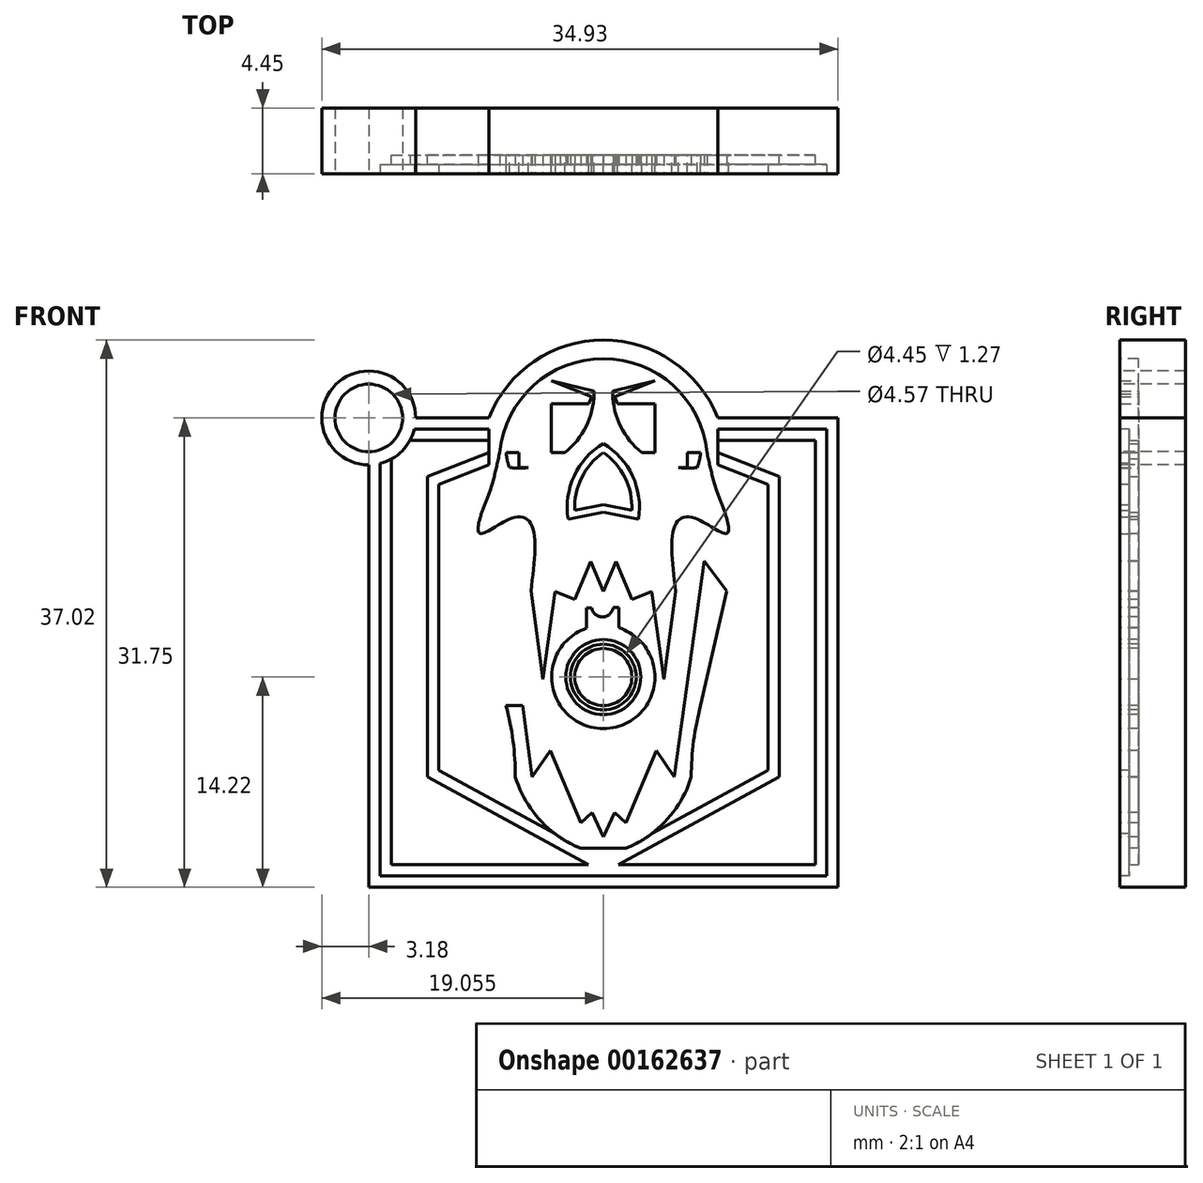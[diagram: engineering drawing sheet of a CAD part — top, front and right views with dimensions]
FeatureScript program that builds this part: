
annotation { "Feature Type Name" : "Feature", "Feature Type Description" : "" }
export const myFeature = defineFeature(function(context is Context, id is Id, definition is map)
    precondition{}
    {
        {
            var Q0;
            Q0=qCreatedBy(makeId("Front.planeOp"),FACE);
            var sketch = newSketch(context, id + "F0", { "sketchPlane" : qUnion([Q0])});
            skLineSegment(sketch, "E0", {"start": v(0, 0) * mm, "end": v(0, 31.75) * mm});
            skLineSegment(sketch, "E1", {"start": v(0, 31.75) * mm, "end": v(31.75, 31.75) * mm});
            skLineSegment(sketch, "E2", {"start": v(31.75, 31.75) * mm, "end": v(31.75, 0) * mm});
            skLineSegment(sketch, "E3", {"start": v(31.75, 0) * mm, "end": v(0, 0) * mm});
            skSolve(sketch);
        }
        {
            var Q0;
            Q0 = qSketchRegion(id + "F0", true);
            extrude(context, id + "F1", {"entities" : qUnion([Q0]), "depth" : 3.17 * mm});
        }
        {
            var Q0;
            Q0=makeQuery(id+"F1.opExtrude","CAP_FACE",FACE,{"disambiguationData":[OSD([sQuery(id+"F0.wireOp",EDGE,"E0"),sQuery(id+"F0.wireOp",EDGE,"E1"),sQuery(id+"F0.wireOp",EDGE,"E2"),sQuery(id+"F0.wireOp",EDGE,"E3")])],"isStart":false});
            var sketch = newSketch(context, id + "F2", { "sketchPlane" : qUnion([Q0])});
            skLineSegment(sketch, "E4", {"start": v(0, 0) * mm, "end": v(15.88, 0) * mm});
            skPoint(sketch, "E5.orphan", {"position": v(0, 15.88) * mm});
            skPoint(sketch, "E6.end.orphan", {"position": v(7.94, 3.97) * mm});
            skPoint(sketch, "E7.start.orphan", {"position": v(0, 7.94) * mm});
            skLineSegment(sketch, "E8", {"start": v(0, 31.75) * mm, "end": v(1.52, 31.75) * mm});
            skLineSegment(sketch, "E9", {"start": v(1.52, 30.23) * mm, "end": v(1.52, 1.52) * mm});
            skLineSegment(sketch, "E10", {"start": v(0, 31.75) * mm, "end": v(0, 27.78) * mm});
            skLineSegment(sketch, "E11.bottom", {"start": v(0, 31.75) * mm, "end": v(31.75, 31.75) * mm});
            skLineSegment(sketch, "E11.top", {"start": v(0, 0) * mm, "end": v(31.75, 0) * mm});
            skLineSegment(sketch, "E11.left", {"start": v(0, 31.75) * mm, "end": v(0, 0) * mm});
            skLineSegment(sketch, "E11.right", {"start": v(31.75, 31.75) * mm, "end": v(31.75, 0) * mm});
            skLineSegment(sketch, "E12.2", {"start": v(30.23, 1.52) * mm, "end": v(30.23, 30.23) * mm});
            skLineSegment(sketch, "E12.3", {"start": v(1.52, 1.52) * mm, "end": v(14.86, 1.52) * mm});
            skPoint(sketch, "E13.orphan", {"position": v(3.97, 31.75) * mm});
            skPoint(sketch, "E14.orphan", {"position": v(15.88, 31.75) * mm});
            skPoint(sketch, "E15.orphan", {"position": v(27.78, 31.75) * mm});
            skPoint(sketch, "E16.orphan", {"position": v(15.88, 0) * mm});
            skLineSegment(sketch, "E17.trimOffspring", {"start": v(16.9, 1.52) * mm, "end": v(30.23, 1.52) * mm});
            skLineSegment(sketch, "E18", {"start": v(3.97, 27.78) * mm, "end": v(3.97, 7.46) * mm});
            skLineSegment(sketch, "E19", {"start": v(27.78, 27.78) * mm, "end": v(27.78, 7.46) * mm});
            skLineSegment(sketch, "E20", {"start": v(3.97, 7.46) * mm, "end": v(14.86, 1.52) * mm});
            skLineSegment(sketch, "E21", {"start": v(27.78, 7.46) * mm, "end": v(16.9, 1.52) * mm});
            skPoint(sketch, "E22.orphan", {"position": v(20.45, 30.23) * mm});
            skPoint(sketch, "E23.orphan", {"position": v(11.3, 30.23) * mm});
            skLineSegment(sketch, "E24", {"start": v(1.52, 30.23) * mm, "end": v(8.13, 30.23) * mm});
            skLineSegment(sketch, "E25", {"start": v(30.23, 30.23) * mm, "end": v(23.62, 30.23) * mm});
            skLineSegment(sketch, "E26", {"start": v(8.13, 30.23) * mm, "end": v(8.13, 29.41) * mm});
            skLineSegment(sketch, "E27", {"start": v(8.13, 29.41) * mm, "end": v(3.97, 27.78) * mm});
            skLineSegment(sketch, "E28", {"start": v(23.62, 30.23) * mm, "end": v(23.62, 29.41) * mm});
            skLineSegment(sketch, "E29", {"start": v(23.62, 29.41) * mm, "end": v(27.78, 27.78) * mm});
            skSolve(sketch);
        }
        {
            var Q0;
            Q0 = qSketchRegion(id + "F2", true);
            extrude(context, id + "F3", {"entities" : qUnion([Q0]), "operationType" : NewBodyOperationType.ADD, "depth" : 1.27 * mm});
        }
        {
            var Q0;
            Q0=makeQuery(id+"F3.opExtrude","CAP_FACE",FACE,{"disambiguationData":[OSD([sQuery(id+"F2.wireOp",EDGE,"E9"),sQuery(id+"F2.wireOp",EDGE,"goVl8tom-Ev7d-GRHB-ppSx-mnuqSaHJAKLd"),sQuery(id+"F2.wireOp",EDGE,"1ae28c5b-480c-4ecc-ba1d-f622eb84b6210.MirrorCS"),sQuery(id+"F2.wireOp",EDGE,"E11.bottom"),sQuery(id+"F2.wireOp",EDGE,"E11.top"),sQuery(id+"F2.wireOp",EDGE,"E11.left"),sQuery(id+"F2.wireOp",EDGE,"E11.right"),sQuery(id+"F2.wireOp",EDGE,"E12.1"),sQuery(id+"F2.wireOp",EDGE,"E12.2"),sQuery(id+"F2.wireOp",EDGE,"E12.3"),sQuery(id+"F2.wireOp",EDGE,"3f8098f8-ebf5-42e8-aa49-ce20f5d09108.trimOffspring"),sQuery(id+"F2.wireOp",EDGE,"E17.trimOffspring"),sQuery(id+"F2.wireOp",EDGE,"E18"),sQuery(id+"F2.wireOp",EDGE,"E19"),sQuery(id+"F2.wireOp",EDGE,"E20"),sQuery(id+"F2.wireOp",EDGE,"E21"),sQuery(id+"F2.wireOp",EDGE,"gHRPagYE-y3ma-9N2y-mR8m-tlt3Iz92IcqW"),sQuery(id+"F2.wireOp",EDGE,"vgOmxDC5-mCE1-dIMU-f8gZ-2gwDJ6tH9BS1"),sQuery(id+"F2.wireOp",EDGE,"jJyTZG4A-tfUV-d1xE-bx1D-zMVtqKziVOon"),sQuery(id+"F2.wireOp",EDGE,"4SgWYagR-BqLy-cmup-oolx-HVRRYwsgYGB8")])],"isStart":false});
            var sketch = newSketch(context, id + "F4", { "sketchPlane" : qUnion([Q0])});
            skLineSegment(sketch, "E30", {"start": v(3.97, 7.46) * mm, "end": v(13.05, 7.46) * mm});
            skLineSegment(sketch, "E31", {"start": v(3.97, 7.46) * mm, "end": v(14.86, 1.52) * mm});
            skLineSegment(sketch, "E32", {"start": v(16.9, 1.52) * mm, "end": v(27.78, 7.46) * mm});
            skLineSegment(sketch, "E33", {"start": v(15.88, 2.63) * mm, "end": v(14.36, 2.63) * mm});
            skLineSegment(sketch, "E34", {"start": v(15.88, 2.63) * mm, "end": v(17.4, 2.63) * mm});
            skPoint(sketch, "E35.end.orphan", {"position": v(15.88, 1.52) * mm});
            skPoint(sketch, "E35.start.orphan", {"position": v(15.88, 0) * mm});
            skLineSegment(sketch, "E36", {"start": v(9.92, 7.46) * mm, "end": v(9.92, 4.22) * mm});
            skLineSegment(sketch, "E37", {"start": v(27.78, 7.46) * mm, "end": v(15.88, 7.46) * mm});
            skLineSegment(sketch, "E38", {"start": v(21.83, 7.46) * mm, "end": v(21.83, 4.22) * mm});
            skPoint(sketch, "E39.end.orphan", {"position": v(15.88, 3.73) * mm});
            skLineSegment(sketch, "E40", {"start": v(3.97, 7.46) * mm, "end": v(3.97, 12.29) * mm});
            skLineSegment(sketch, "E41", {"start": v(3.97, 12.29) * mm, "end": v(12.97, 12.29) * mm});
            skLineSegment(sketch, "E42", {"start": v(9.92, 7.46) * mm, "end": v(9.92, 12.29) * mm});
            skLineSegment(sketch, "E43", {"start": v(21.83, 7.46) * mm, "end": v(21.83, 12.29) * mm});
            skLineSegment(sketch, "E44", {"start": v(3.97, 27.78) * mm, "end": v(3.97, 12.29) * mm});
            skLineSegment(sketch, "E45", {"start": v(9.92, 12.29) * mm, "end": v(9.29, 12.29) * mm});
            skLineSegment(sketch, "E46", {"start": v(21.83, 12.29) * mm, "end": v(22.46, 12.29) * mm});
            skArc(sketch, "E47", {"start": v(9.92, 7.46) * mm, "mid": v(9.76, 9.9) * mm, "end": v(9.29, 12.29) * mm});
            skArc(sketch, "E48", {"start": v(22.46, 12.29) * mm, "mid": v(21.99, 9.9) * mm, "end": v(21.83, 7.46) * mm});
            skLineSegment(sketch, "E49", {"start": v(3.97, 20.03) * mm, "end": v(7.52, 20.03) * mm});
            skLineSegment(sketch, "E50", {"start": v(27.78, 20.03) * mm, "end": v(27.78, 12.29) * mm});
            skLineSegment(sketch, "E51", {"start": v(7.52, 20.03) * mm, "end": v(9.29, 12.29) * mm});
            skLineSegment(sketch, "E52", {"start": v(27.78, 20.03) * mm, "end": v(24.23, 20.03) * mm});
            skLineSegment(sketch, "E53", {"start": v(24.23, 20.03) * mm, "end": v(22.46, 12.29) * mm});
            skLineSegment(sketch, "E54", {"start": v(7.52, 20.03) * mm, "end": v(9.06, 22.06) * mm});
            skLineSegment(sketch, "E55", {"start": v(24.23, 20.03) * mm, "end": v(22.7, 22.06) * mm});
            skLineSegment(sketch, "E56", {"start": v(9.06, 22.06) * mm, "end": v(11.06, 7.46) * mm});
            skLineSegment(sketch, "E57", {"start": v(22.7, 22.06) * mm, "end": v(20.69, 7.46) * mm});
            skLineSegment(sketch, "E58", {"start": v(15.88, 2.63) * mm, "end": v(15.88, 3.39) * mm});
            skLineSegment(sketch, "E59", {"start": v(15.88, 7.46) * mm, "end": v(13.94, 7.46) * mm});
            skLineSegment(sketch, "E60", {"start": v(3.97, 7.46) * mm, "end": v(6.69, 5.98) * mm});
            skLineSegment(sketch, "E61", {"start": v(15.88, 7.46) * mm, "end": v(20.69, 7.46) * mm});
            skLineSegment(sketch, "E62", {"start": v(14.36, 2.63) * mm, "end": v(14.36, 4.36) * mm});
            skArc(sketch, "E63", {"start": v(9.92, 7.46) * mm, "mid": v(11.6, 4.54) * mm, "end": v(14.36, 2.63) * mm});
            skLineSegment(sketch, "E64", {"start": v(17.4, 2.63) * mm, "end": v(17.4, 4.36) * mm});
            skArc(sketch, "E65", {"start": v(17.4, 2.63) * mm, "mid": v(20.16, 4.54) * mm, "end": v(21.83, 7.46) * mm});
            skLineSegment(sketch, "E66", {"start": v(11.06, 7.46) * mm, "end": v(11.06, 5.19) * mm});
            skLineSegment(sketch, "E67", {"start": v(20.69, 7.46) * mm, "end": v(20.69, 5.19) * mm});
            skLineSegment(sketch, "E68", {"start": v(14.36, 7.46) * mm, "end": v(11.06, 7.46) * mm});
            skLineSegment(sketch, "E69", {"start": v(12.7, 7.46) * mm, "end": v(12.7, 3.54) * mm});
            skLineSegment(sketch, "E70", {"start": v(17.4, 7.46) * mm, "end": v(20.69, 7.46) * mm});
            skLineSegment(sketch, "E71", {"start": v(19.04, 7.46) * mm, "end": v(19.04, 3.54) * mm});
            skLineSegment(sketch, "E72", {"start": v(11.06, 7.46) * mm, "end": v(12.7, 7.46) * mm});
            skLineSegment(sketch, "E73", {"start": v(14.36, 7.46) * mm, "end": v(12.7, 7.46) * mm});
            skLineSegment(sketch, "E74", {"start": v(13.53, 6.31) * mm, "end": v(13.53, 4.92) * mm});
            skLineSegment(sketch, "E75", {"start": v(20.69, 7.46) * mm, "end": v(19.04, 7.46) * mm});
            skLineSegment(sketch, "E76", {"start": v(19.04, 7.46) * mm, "end": v(17.4, 7.46) * mm});
            skLineSegment(sketch, "E77", {"start": v(11.06, 5.19) * mm, "end": v(12.7, 5.19) * mm});
            skLineSegment(sketch, "E78", {"start": v(12.7, 5.19) * mm, "end": v(12.7, 3.54) * mm});
            skLineSegment(sketch, "E79", {"start": v(12.7, 4.36) * mm, "end": v(11.76, 4.36) * mm});
            skLineSegment(sketch, "E80", {"start": v(12.7, 7.46) * mm, "end": v(13.05, 7.46) * mm});
            skLineSegment(sketch, "E81", {"start": v(13.12, 7.29) * mm, "end": v(13.12, 3.26) * mm});
            skLineSegment(sketch, "E82", {"start": v(12.7, 4.36) * mm, "end": v(13.12, 4.36) * mm});
            skLineSegment(sketch, "E83", {"start": v(19.04, 7.46) * mm, "end": v(18.22, 7.46) * mm});
            skLineSegment(sketch, "E84", {"start": v(18.63, 7.29) * mm, "end": v(18.63, 3.26) * mm});
            skLineSegment(sketch, "E85", {"start": v(20.69, 5.19) * mm, "end": v(19.04, 5.19) * mm});
            skLineSegment(sketch, "E86", {"start": v(19.04, 5.19) * mm, "end": v(19.04, 3.54) * mm});
            skLineSegment(sketch, "E87", {"start": v(19.04, 4.36) * mm, "end": v(19.99, 4.36) * mm});
            skLineSegment(sketch, "E88", {"start": v(19.04, 4.36) * mm, "end": v(18.63, 4.36) * mm});
            skLineSegment(sketch, "E89", {"start": v(13.53, 7.46) * mm, "end": v(14.36, 7.46) * mm});
            skLineSegment(sketch, "E90", {"start": v(13.94, 5.34) * mm, "end": v(13.94, 2.8) * mm});
            skLineSegment(sketch, "E91", {"start": v(18.22, 7.46) * mm, "end": v(17.4, 7.46) * mm});
            skLineSegment(sketch, "E92", {"start": v(17.8, 5.34) * mm, "end": v(17.8, 2.8) * mm});
            skLineSegment(sketch, "E93", {"start": v(18.22, 6.31) * mm, "end": v(18.22, 4.92) * mm});
            skLineSegment(sketch, "E94", {"start": v(11.89, 7.46) * mm, "end": v(12.7, 7.46) * mm});
            skLineSegment(sketch, "E95", {"start": v(12.3, 7.46) * mm, "end": v(12.3, 9.24) * mm});
            skLineSegment(sketch, "E96", {"start": v(13.12, 4.36) * mm, "end": v(14.36, 4.36) * mm});
            skLineSegment(sketch, "E97", {"start": v(18.63, 4.36) * mm, "end": v(17.4, 4.36) * mm});
            skLineSegment(sketch, "E98", {"start": v(15.88, 7.46) * mm, "end": v(15.88, 5.04) * mm});
            skLineSegment(sketch, "E99", {"start": v(19.86, 7.46) * mm, "end": v(19.04, 7.46) * mm});
            skLineSegment(sketch, "E100", {"start": v(19.45, 7.46) * mm, "end": v(19.45, 9.24) * mm});
            skPoint(sketch, "E100.endSnap0", {"position": v(19.45, 7.46) * mm});
            skLineSegment(sketch, "E101", {"start": v(13.53, 4.92) * mm, "end": v(13.53, 3.02) * mm});
            skPoint(sketch, "E102.endSnap0", {"position": v(13.74, 4.36) * mm});
            skLineSegment(sketch, "E103", {"start": v(18.22, 4.92) * mm, "end": v(18.22, 3.02) * mm});
            skPoint(sketch, "E104.orphan", {"position": v(12.84, 2.63) * mm});
            skPoint(sketch, "E105.orphan", {"position": v(18.91, 2.63) * mm});
            skLineSegment(sketch, "E106", {"start": v(15.88, 6.25) * mm, "end": v(15.88, 5.04) * mm});
            skLineSegment(sketch, "E107", {"start": v(15.88, 5.65) * mm, "end": v(15.88, 5.04) * mm});
            skLineSegment(sketch, "E108", {"start": v(14.36, 3.5) * mm, "end": v(12.7, 3.54) * mm});
            skLineSegment(sketch, "E109", {"start": v(19.04, 3.54) * mm, "end": v(17.4, 3.54) * mm});
            skLineSegment(sketch, "E110", {"start": v(20.69, 7.46) * mm, "end": v(19.45, 9.24) * mm});
            skLineSegment(sketch, "E111", {"start": v(15.88, 3.39) * mm, "end": v(16.63, 5.04) * mm});
            skLineSegment(sketch, "E112", {"start": v(11.06, 7.46) * mm, "end": v(12.3, 9.24) * mm});
            skLineSegment(sketch, "E113", {"start": v(15.12, 5.04) * mm, "end": v(15.88, 3.39) * mm});
            skLineSegment(sketch, "E114", {"start": v(15.12, 5.04) * mm, "end": v(14.36, 4.36) * mm});
            skLineSegment(sketch, "E115", {"start": v(12.3, 9.24) * mm, "end": v(14.36, 4.36) * mm});
            skLineSegment(sketch, "E116", {"start": v(16.63, 5.04) * mm, "end": v(17.4, 4.36) * mm});
            skLineSegment(sketch, "E117", {"start": v(17.4, 4.36) * mm, "end": v(19.45, 9.24) * mm});
            skLineSegment(sketch, "E118.trimOffspring", {"start": v(13.94, 7.46) * mm, "end": v(15.88, 7.46) * mm});
            skLineSegment(sketch, "E119.trimOffspring", {"start": v(13.94, 7.46) * mm, "end": v(27.78, 7.46) * mm});
            skPoint(sketch, "E120.orphan", {"position": v(13.12, 7.46) * mm});
            skLineSegment(sketch, "E121.trimOffspring", {"start": v(13.53, 7.46) * mm, "end": v(11.06, 7.46) * mm});
            skPoint(sketch, "E122.start.orphan", {"position": v(15.88, 5.35) * mm});
            skPoint(sketch, "E123.orphan", {"position": v(14.36, 5.04) * mm});
            skPoint(sketch, "E124.start.orphan", {"position": v(17.4, 5.04) * mm});
            skPoint(sketch, "E125.start.orphan", {"position": v(16.63, 3.84) * mm});
            skPoint(sketch, "E126.orphan", {"position": v(16.63, 4.44) * mm});
            skPoint(sketch, "E127.end.orphan", {"position": v(16.63, 2.63) * mm});
            skPoint(sketch, "E128.orphan", {"position": v(17.8, 7.46) * mm});
            skPoint(sketch, "E129.orphan", {"position": v(18.63, 7.46) * mm});
            skPoint(sketch, "E130.orphan", {"position": v(17.4, 4.44) * mm});
            skLineSegment(sketch, "E131.trimOffspring", {"start": v(24.23, 20.03) * mm, "end": v(27.78, 20.03) * mm});
            skCircle(sketch, "E132", {"center": v(15.87, 14.22) * mm, "radius": 1.93 * mm});
            skCircle(sketch, "E133", {"center": v(15.87, 14.22) * mm, "radius": 2.22 * mm});
            skCircle(sketch, "E134", {"center": v(15.87, 14.22) * mm, "radius": 2.54 * mm});
            skArc(sketch, "E135", {"start": v(14.72, 17.52) * mm, "mid": v(15.93, 10.73) * mm, "end": v(16.91, 17.55) * mm});
            skLineSegment(sketch, "E136.trimOffspring", {"start": v(18.78, 12.29) * mm, "end": v(27.78, 12.29) * mm});
            skLineSegment(sketch, "E137.trimOffspring", {"start": v(12.96, 12.3) * mm, "end": v(12.96, 12.29) * mm});
            skLineSegment(sketch, "E138.trimOffspring", {"start": v(18.79, 12.3) * mm, "end": v(18.79, 12.29) * mm});
            skLineSegment(sketch, "E139", {"start": v(15.02, 22.04) * mm, "end": v(15.87, 20.02) * mm});
            skLineSegment(sketch, "E140", {"start": v(16.73, 22.04) * mm, "end": v(15.87, 20.02) * mm});
            skLineSegment(sketch, "E141", {"start": v(10.97, 20.02) * mm, "end": v(11.79, 14.07) * mm});
            skLineSegment(sketch, "E142", {"start": v(20.78, 20.01) * mm, "end": v(19.96, 14.06) * mm});
            skLineSegment(sketch, "E143", {"start": v(11.79, 14.07) * mm, "end": v(12.6, 20.02) * mm});
            skLineSegment(sketch, "E144", {"start": v(19.96, 14.06) * mm, "end": v(19.14, 20.01) * mm});
            skLineSegment(sketch, "E145", {"start": v(17.61, 20.53) * mm, "end": v(17.69, 20.5) * mm});
            skPoint(sketch, "E146.endSnap0", {"position": v(13.94, 20.02) * mm});
            skLineSegment(sketch, "E147", {"start": v(12.6, 20.02) * mm, "end": v(13.94, 19.46) * mm});
            skPoint(sketch, "E148.endSnap0", {"position": v(17.8, 20.47) * mm});
            skLineSegment(sketch, "E149", {"start": v(17.8, 19.45) * mm, "end": v(19.14, 20.01) * mm});
            skLineSegment(sketch, "E150", {"start": v(14.72, 17.52) * mm, "end": v(14.72, 18.9) * mm});
            skLineSegment(sketch, "E151", {"start": v(14.72, 18.9) * mm, "end": v(15.1, 18.9) * mm});
            skLineSegment(sketch, "E152", {"start": v(16.91, 17.55) * mm, "end": v(16.91, 18.92) * mm});
            skLineSegment(sketch, "E153", {"start": v(16.91, 18.92) * mm, "end": v(16.54, 18.92) * mm});
            skArc(sketch, "E154", {"start": v(15.1, 18.9) * mm, "mid": v(15.83, 18.29) * mm, "end": v(16.54, 18.92) * mm});
            skPoint(sketch, "E155.orphan", {"position": v(9.34, 20.03) * mm});
            skPoint(sketch, "E156.orphan", {"position": v(22.4, 20) * mm});
            skPoint(sketch, "E157.orphan", {"position": v(15.87, 18.87) * mm});
            skPoint(sketch, "E158.orphan", {"position": v(14.2, 20.02) * mm});
            skPoint(sketch, "E159.end.orphan", {"position": v(14.74, 20.02) * mm});
            skPoint(sketch, "E160.start.orphan", {"position": v(19.96, 20.01) * mm});
            skPoint(sketch, "E161.end.orphan", {"position": v(19.96, 14.93) * mm});
            skPoint(sketch, "E162.orphan", {"position": v(11.79, 20.02) * mm});
            skPoint(sketch, "E163.orphan", {"position": v(13.67, 20.02) * mm});
            skPoint(sketch, "E164.end.orphan", {"position": v(15.87, 17.71) * mm});
            skPoint(sketch, "E164.start.orphan", {"position": v(15.87, 18.29) * mm});
            skPoint(sketch, "E165.trimOffspring.end.orphan", {"position": v(15.87, 16.15) * mm});
            skPoint(sketch, "E166.orphan", {"position": v(15.88, 12.29) * mm});
            skPoint(sketch, "E167.orphan", {"position": v(17.2, 20.68) * mm});
            skPoint(sketch, "E168.orphan", {"position": v(17.93, 20.43) * mm});
            skLineSegment(sketch, "E169.trimOffspring", {"start": v(17.69, 20.5) * mm, "end": v(17.61, 20.53) * mm});
            skPoint(sketch, "E170.trimOffspring.end.orphan", {"position": v(18.17, 20.34) * mm});
            skPoint(sketch, "E171.orphan", {"position": v(19.28, 22.06) * mm});
            skPoint(sketch, "E172.end.orphan", {"position": v(17.58, 22.06) * mm});
            skLineSegment(sketch, "E173", {"start": v(8.86, 29.41) * mm, "end": v(8.86, 35.76) * mm});
            skLineSegment(sketch, "E174", {"start": v(22.9, 29.41) * mm, "end": v(22.9, 35.76) * mm});
            skPoint(sketch, "E174.endSnap0", {"position": v(22.9, 29.82) * mm});
            skLineSegment(sketch, "E175", {"start": v(22.9, 35.76) * mm, "end": v(8.86, 35.76) * mm});
            skLineSegment(sketch, "E176", {"start": v(15.87, 35.76) * mm, "end": v(15.88, 31.75) * mm});
            skArc(sketch, "E177", {"start": v(22.9, 29.41) * mm, "mid": v(15.87, 35.76) * mm, "end": v(8.86, 29.41) * mm});
            skPoint(sketch, "E178.endSnap0", {"position": v(10.98, 24.59) * mm});
            skPoint(sketch, "E179.orphan", {"position": v(25.26, 25.64) * mm});
            skPoint(sketch, "E180.end.orphan", {"position": v(10.32, 21.82) * mm});
            skPoint(sketch, "E181.end.orphan", {"position": v(9.66, 24.97) * mm});
            skPoint(sketch, "E182.end.orphan", {"position": v(21.46, 21.81) * mm});
            skPoint(sketch, "E183.end.orphan", {"position": v(22.15, 25.22) * mm});
            skPoint(sketch, "E184.end.orphan", {"position": v(12.9, 27.12) * mm});
            skPoint(sketch, "E185.orphan", {"position": v(26.11, 28.34) * mm});
            skPoint(sketch, "E186.orphan", {"position": v(5.64, 28.34) * mm});
            skPoint(sketch, "E187.end.orphan", {"position": v(25.26, 24.6) * mm});
            skPoint(sketch, "E188.end.orphan", {"position": v(11.79, 14.94) * mm});
            skLineSegment(sketch, "E189", {"start": v(8.86, 29.41) * mm, "end": v(8.86, 26.87) * mm});
            skLineSegment(sketch, "E190", {"start": v(8.86, 26.87) * mm, "end": v(8.22, 26.87) * mm});
            skLineSegment(sketch, "E191", {"start": v(8.22, 26.87) * mm, "end": v(8.22, 24.97) * mm});
            skLineSegment(sketch, "E192", {"start": v(8.22, 24.97) * mm, "end": v(7.52, 24.97) * mm});
            skFitSpline(sketch, "E193", {"points": [v(8.86, 29.41) * mm, v(8.22, 26.87) * mm, v(7.52, 24.97) * mm, v(7.52, 23.93) * mm, v(9.66, 24.97) * mm, v(10.98, 24.59) * mm, v(10.97, 20.02) * mm], "startDerivative": vector(-3.1, -14.67) * mm, "endDerivative": vector(-2.94, -23.33) * mm});
            skLineSegment(sketch, "E194", {"start": v(22.9, 29.41) * mm, "end": v(22.9, 26.87) * mm});
            skLineSegment(sketch, "E195", {"start": v(22.9, 26.87) * mm, "end": v(23.53, 26.87) * mm});
            skLineSegment(sketch, "E196", {"start": v(23.53, 26.87) * mm, "end": v(23.53, 24.97) * mm});
            skLineSegment(sketch, "E197", {"start": v(23.53, 24.97) * mm, "end": v(24.23, 24.97) * mm});
            skLineSegment(sketch, "E198", {"start": v(9.66, 24.97) * mm, "end": v(8.22, 24.97) * mm});
            skLineSegment(sketch, "E199", {"start": v(23.53, 24.97) * mm, "end": v(22.09, 24.97) * mm});
            skPoint(sketch, "E200.endSnap0", {"position": v(9.66, 24.78) * mm});
            skFitSpline(sketch, "E201", {"points": [v(22.9, 29.41) * mm, v(23.53, 26.87) * mm, v(24.23, 24.97) * mm, v(24.23, 23.93) * mm, v(22.09, 24.97) * mm, v(20.77, 24.59) * mm, v(20.78, 20.01) * mm], "startDerivative": vector(3.1, -14.64) * mm, "endDerivative": vector(2.95, -23.36) * mm});
            skLineSegment(sketch, "E202", {"start": v(15.02, 22.04) * mm, "end": v(13.94, 19.46) * mm});
            skLineSegment(sketch, "E203", {"start": v(16.73, 22.04) * mm, "end": v(17.8, 19.45) * mm});
            skSolve(sketch);
        }
        {
            var Q0;
            Q0=makeQuery(id+"F3.boolean.opBoolean","MERGE",FACE,{"derivedFrom":[makeQuery(id+"F1.opExtrude","SWEPT_FACE",FACE,{"disambiguationData":[OSD([sQuery(id+"F0.wireOp",EDGE,"E1")])]}),makeQuery(id+"F3.opExtrude","SWEPT_FACE",FACE,{"disambiguationData":[OSD([sQuery(id+"F2.wireOp",EDGE,"E11.bottom")])]})]});
            var sketch = newSketch(context, id + "F5", { "sketchPlane" : qUnion([Q0])});
            skLineSegment(sketch, "E204", {"start": v(0, 0) * mm, "end": v(6.35, 0) * mm});
            skLineSegment(sketch, "E205", {"start": v(31.75, -4.45) * mm, "end": v(25.4, -4.45) * mm});
            skLineSegment(sketch, "E206.bottom", {"start": v(6.35, 0) * mm, "end": v(25.4, 0) * mm});
            skLineSegment(sketch, "E206.top", {"start": v(6.35, -4.45) * mm, "end": v(25.4, -4.45) * mm});
            skLineSegment(sketch, "E206.left", {"start": v(6.35, 0) * mm, "end": v(6.35, -4.45) * mm});
            skLineSegment(sketch, "E206.right", {"start": v(25.4, 0) * mm, "end": v(25.4, -4.45) * mm});
            skSolve(sketch);
        }
        {
            var Q0;
            Q0 = qSketchRegion(id + "F5", true);
            extrude(context, id + "F6", {"entities" : qUnion([Q0]), "operationType" : NewBodyOperationType.ADD, "depth" : 12.7 * mm});
        }
        {
            var Q0;
            {var subQ0=sQuery(id+"F4.wireOp",EDGE,"E189");Q0=makeQuery(id+"F4.imprint","IMPRINT",FACE,{"disambiguationData":[TD([[makeQuery(id+"F4.imprint","IMPRINT",EDGE,{"derivedFrom":subQ0}),-1.0]])]});}
            var Q1;
            {var subQ0=sQuery(id+"F4.wireOp",EDGE,"E194");Q1=makeQuery(id+"F4.imprint","IMPRINT",FACE,{"disambiguationData":[TD([[makeQuery(id+"F4.imprint","IMPRINT",EDGE,{"derivedFrom":subQ0}),1.0]])]});}
            var Q2;
            {var subQ0=sQuery(id+"F4.wireOp",EDGE,"E66");Q2=makeQuery(id+"F4.imprint","IMPRINT",FACE,{"disambiguationData":[TD([[makeQuery(id+"F4.imprint","IMPRINT",EDGE,{"derivedFrom":subQ0}),-1.0]])]});}
            var Q3;
            {var subQ3=sQuery(id+"F4.wireOp",EDGE,"E137.trimOffspring");Q3=makeQuery(id+"F4.imprint","IMPRINT",FACE,{"disambiguationData":[TD([[makeQuery(id+"F4.imprint","IMPRINT",EDGE,{"derivedFrom":subQ3}),1.0]])]});}
            var Q4;
            Q4=makeQuery(id+"F4.imprint","IMPRINT",FACE,{"disambiguationData":[TD([[makeQuery(id+"F4.imprint","IMPRINT",EDGE,{"derivedFrom":sQuery(id+"F4.wireOp",EDGE,"E42")}),1.0]])]});
            var Q5;
            {var subQ0=sQuery(id+"F4.wireOp",EDGE,"E43");Q5=makeQuery(id+"F4.imprint","IMPRINT",FACE,{"disambiguationData":[TD([[makeQuery(id+"F4.imprint","IMPRINT",EDGE,{"derivedFrom":subQ0}),-1.0]])]});}
            var Q6;
            {var subQ3=sQuery(id+"F4.wireOp",EDGE,"E79");Q6=makeQuery(id+"F4.imprint","IMPRINT",FACE,{"disambiguationData":[TD([[makeQuery(id+"F4.imprint","IMPRINT",EDGE,{"derivedFrom":subQ3}),1.0]])]});}
            var Q7;
            {var subQ1=sQuery(id+"F4.wireOp",EDGE,"E63");var subQ3=sQuery(id+"F4.wireOp",EDGE,"E81");var subQ4=makeQuery(id+"F4.imprint","INTERSECT",VERTEX,{"derivedFrom":[subQ1,subQ3]});Q7=makeQuery(id+"F4.imprint","IMPRINT",FACE,{"disambiguationData":[TD([[makeQuery(id+"F4.imprint","IMPRINT",EDGE,{"disambiguationData":[TD([[subQ4,1.0]])],"derivedFrom":subQ3}),-1.0]])]});}
            var Q8;
            {var subQ0=sQuery(id+"F4.wireOp",EDGE,"E84");var subQ1=sQuery(id+"F4.wireOp",EDGE,"E65");var subQ2=makeQuery(id+"F4.imprint","INTERSECT",VERTEX,{"derivedFrom":[subQ1,subQ0]});Q8=makeQuery(id+"F4.imprint","IMPRINT",FACE,{"disambiguationData":[TD([[makeQuery(id+"F4.imprint","IMPRINT",EDGE,{"disambiguationData":[TD([[subQ2,1.0]])],"derivedFrom":subQ0}),1.0]])]});}
            var Q9;
            {var subQ3=sQuery(id+"F4.wireOp",EDGE,"E87");Q9=makeQuery(id+"F4.imprint","IMPRINT",FACE,{"disambiguationData":[TD([[makeQuery(id+"F4.imprint","IMPRINT",EDGE,{"derivedFrom":subQ3}),-1.0]])]});}
            var Q10;
            {var subQ3=sQuery(id+"F4.wireOp",EDGE,"E67");Q10=makeQuery(id+"F4.imprint","IMPRINT",FACE,{"disambiguationData":[TD([[makeQuery(id+"F4.imprint","IMPRINT",EDGE,{"derivedFrom":subQ3}),1.0]])]});}
            var Q11;
            {var subQ3=sQuery(id+"F4.wireOp",EDGE,"E138.trimOffspring");Q11=makeQuery(id+"F4.imprint","IMPRINT",FACE,{"disambiguationData":[TD([[makeQuery(id+"F4.imprint","IMPRINT",EDGE,{"derivedFrom":subQ3}),-1.0]])]});}
            var Q12;
            {var subQ0=sQuery(id+"F4.wireOp",EDGE,"E191");Q12=makeQuery(id+"F4.imprint","IMPRINT",FACE,{"disambiguationData":[TD([[makeQuery(id+"F4.imprint","IMPRINT",EDGE,{"derivedFrom":subQ0}),-1.0]])]});}
            var Q13;
            {var subQ0=sQuery(id+"F4.wireOp",EDGE,"E192");Q13=makeQuery(id+"F4.imprint","IMPRINT",FACE,{"disambiguationData":[TD([[makeQuery(id+"F4.imprint","IMPRINT",EDGE,{"derivedFrom":subQ0}),1.0]])]});}
            var Q14;
            {var subQ0=sQuery(id+"F4.wireOp",EDGE,"E196");Q14=makeQuery(id+"F4.imprint","IMPRINT",FACE,{"disambiguationData":[TD([[makeQuery(id+"F4.imprint","IMPRINT",EDGE,{"derivedFrom":subQ0}),1.0]])]});}
            var Q15;
            {var subQ0=sQuery(id+"F4.wireOp",EDGE,"E197");Q15=makeQuery(id+"F4.imprint","IMPRINT",FACE,{"disambiguationData":[TD([[makeQuery(id+"F4.imprint","IMPRINT",EDGE,{"derivedFrom":subQ0}),-1.0]])]});}
            var Q16;
            {var subQ3=sQuery(id+"F4.wireOp",EDGE,"E42");Q16=makeQuery(id+"F4.imprint","IMPRINT",FACE,{"disambiguationData":[TD([[makeQuery(id+"F4.imprint","IMPRINT",EDGE,{"derivedFrom":subQ3}),-1.0]])]});}
            var Q17;
            {var subQ0=sQuery(id+"F4.wireOp",EDGE,"E45");Q17=makeQuery(id+"F4.imprint","IMPRINT",FACE,{"disambiguationData":[TD([[makeQuery(id+"F4.imprint","IMPRINT",EDGE,{"derivedFrom":subQ0}),-1.0]])]});}
            var Q18;
            {var subQ0=sQuery(id+"F4.wireOp",EDGE,"E43");Q18=makeQuery(id+"F4.imprint","IMPRINT",FACE,{"disambiguationData":[TD([[makeQuery(id+"F4.imprint","IMPRINT",EDGE,{"derivedFrom":subQ0}),1.0]])]});}
            var Q19;
            {var subQ4=sQuery(id+"F4.wireOp",EDGE,"E53");Q19=makeQuery(id+"F4.imprint","IMPRINT",FACE,{"disambiguationData":[TD([[makeQuery(id+"F4.imprint","IMPRINT",EDGE,{"derivedFrom":subQ4}),-1.0]])]});}
            var Q20;
            {var subQ0=sQuery(id+"F4.wireOp",EDGE,"E77");Q20=makeQuery(id+"F4.imprint","IMPRINT",FACE,{"disambiguationData":[TD([[makeQuery(id+"F4.imprint","IMPRINT",EDGE,{"derivedFrom":subQ0}),-1.0]])]});}
            var Q21;
            {var subQ0=sQuery(id+"F4.wireOp",EDGE,"E81");var subQ1=sQuery(id+"F4.wireOp",EDGE,"E63");var subQ2=makeQuery(id+"F4.imprint","INTERSECT",VERTEX,{"derivedFrom":[subQ1,subQ0]});Q21=makeQuery(id+"F4.imprint","IMPRINT",FACE,{"disambiguationData":[TD([[makeQuery(id+"F4.imprint","IMPRINT",EDGE,{"disambiguationData":[TD([[subQ2,-1.0]])],"derivedFrom":subQ1}),1.0]])]});}
            var Q22;
            {var subQ0=sQuery(id+"F4.wireOp",EDGE,"E90");var subQ1=sQuery(id+"F4.wireOp",EDGE,"E63");var subQ2=makeQuery(id+"F4.imprint","INTERSECT",VERTEX,{"derivedFrom":[subQ1,subQ0]});Q22=makeQuery(id+"F4.imprint","IMPRINT",FACE,{"disambiguationData":[TD([[makeQuery(id+"F4.imprint","IMPRINT",EDGE,{"disambiguationData":[TD([[subQ2,1.0]])],"derivedFrom":subQ1}),1.0]])]});}
            var Q23;
            {var subQ1=sQuery(id+"F4.wireOp",EDGE,"E63");var subQ3=sQuery(id+"F4.wireOp",EDGE,"E90");var subQ4=makeQuery(id+"F4.imprint","INTERSECT",VERTEX,{"derivedFrom":[subQ1,subQ3]});Q23=makeQuery(id+"F4.imprint","IMPRINT",FACE,{"disambiguationData":[TD([[makeQuery(id+"F4.imprint","IMPRINT",EDGE,{"disambiguationData":[TD([[subQ4,1.0]])],"derivedFrom":subQ3}),1.0]])]});}
            var Q24;
            {var subQ0=sQuery(id+"F4.wireOp",EDGE,"E65");var subQ5=sQuery(id+"F4.wireOp",EDGE,"E92");var subQ6=makeQuery(id+"F4.imprint","INTERSECT",VERTEX,{"derivedFrom":[subQ0,subQ5]});Q24=makeQuery(id+"F4.imprint","IMPRINT",FACE,{"disambiguationData":[TD([[makeQuery(id+"F4.imprint","IMPRINT",EDGE,{"disambiguationData":[TD([[subQ6,1.0]])],"derivedFrom":subQ5}),-1.0]])]});}
            var Q25;
            {var subQ0=sQuery(id+"F4.wireOp",EDGE,"E92");var subQ1=sQuery(id+"F4.wireOp",EDGE,"E65");var subQ2=makeQuery(id+"F4.imprint","INTERSECT",VERTEX,{"derivedFrom":[subQ1,subQ0]});Q25=makeQuery(id+"F4.imprint","IMPRINT",FACE,{"disambiguationData":[TD([[makeQuery(id+"F4.imprint","IMPRINT",EDGE,{"disambiguationData":[TD([[subQ2,-1.0]])],"derivedFrom":subQ1}),1.0]])]});}
            var Q26;
            {var subQ0=sQuery(id+"F4.wireOp",EDGE,"E84");var subQ1=sQuery(id+"F4.wireOp",EDGE,"E65");var subQ2=makeQuery(id+"F4.imprint","INTERSECT",VERTEX,{"derivedFrom":[subQ1,subQ0]});Q26=makeQuery(id+"F4.imprint","IMPRINT",FACE,{"disambiguationData":[TD([[makeQuery(id+"F4.imprint","IMPRINT",EDGE,{"disambiguationData":[TD([[subQ2,1.0]])],"derivedFrom":subQ1}),1.0]])]});}
            var Q27;
            {var subQ0=sQuery(id+"F4.wireOp",EDGE,"E85");Q27=makeQuery(id+"F4.imprint","IMPRINT",FACE,{"disambiguationData":[TD([[makeQuery(id+"F4.imprint","IMPRINT",EDGE,{"derivedFrom":subQ0}),1.0]])]});}
            var Q28;
            {var subQ3=sQuery(id+"F4.wireOp",EDGE,"E82");Q28=makeQuery(id+"F4.imprint","IMPRINT",FACE,{"disambiguationData":[TD([[makeQuery(id+"F4.imprint","IMPRINT",EDGE,{"derivedFrom":subQ3}),-1.0]])]});}
            var Q29;
            {var subQ0=sQuery(id+"F4.wireOp",EDGE,"E88");Q29=makeQuery(id+"F4.imprint","IMPRINT",FACE,{"disambiguationData":[TD([[makeQuery(id+"F4.imprint","IMPRINT",EDGE,{"derivedFrom":subQ0}),1.0]])]});}
            var Q30;
            {var subQ3=sQuery(id+"F4.wireOp",EDGE,"E33");Q30=makeQuery(id+"F4.imprint","IMPRINT",FACE,{"disambiguationData":[TD([[makeQuery(id+"F4.imprint","IMPRINT",EDGE,{"derivedFrom":subQ3}),-1.0]])]});}
            var Q31;
            {var subQ3=sQuery(id+"F4.wireOp",EDGE,"E34");Q31=makeQuery(id+"F4.imprint","IMPRINT",FACE,{"disambiguationData":[TD([[makeQuery(id+"F4.imprint","IMPRINT",EDGE,{"derivedFrom":subQ3}),1.0]])]});}
            var Q32;
            {var subQ2=sQuery(id+"F4.wireOp",EDGE,"E66");Q32=makeQuery(id+"F4.imprint","IMPRINT",FACE,{"disambiguationData":[TD([[makeQuery(id+"F4.imprint","IMPRINT",EDGE,{"derivedFrom":subQ2}),1.0]])]});}
            var Q33;
            {var subQ4=sQuery(id+"F4.wireOp",EDGE,"E67");Q33=makeQuery(id+"F4.imprint","IMPRINT",FACE,{"disambiguationData":[TD([[makeQuery(id+"F4.imprint","IMPRINT",EDGE,{"derivedFrom":subQ4}),-1.0]])]});}
            var Q34;
            Q34=makeQuery(id+"F4.imprint","IMPRINT",FACE,{"disambiguationData":[TD([[makeQuery(id+"F4.imprint","IMPRINT",EDGE,{"derivedFrom":sQuery(id+"F4.wireOp",EDGE,"E134")}),-1.0]])]});
            var Q35;
            {var subQ0=sQuery(id+"F4.wireOp",EDGE,"E176");Q35=makeQuery(id+"F4.imprint","IMPRINT",FACE,{"disambiguationData":[TD([[makeQuery(id+"F4.imprint","IMPRINT",EDGE,{"derivedFrom":subQ0}),1.0]])]});}
            var Q36;
            {var subQ0=sQuery(id+"F4.wireOp",EDGE,"E176");Q36=makeQuery(id+"F4.imprint","IMPRINT",FACE,{"disambiguationData":[TD([[makeQuery(id+"F4.imprint","IMPRINT",EDGE,{"derivedFrom":subQ0}),-1.0]])]});}
            var Q37;
            Q37=makeQuery(id+"F4.imprint","IMPRINT",FACE,{"disambiguationData":[TD([[makeQuery(id+"F4.imprint","IMPRINT",EDGE,{"derivedFrom":sQuery(id+"F4.wireOp",EDGE,"E139")}),1.0]])]});
            var Q38;
            {var subQ0=sQuery(id+"F4.wireOp",EDGE,"E100");Q38=makeQuery(id+"F4.imprint","IMPRINT",FACE,{"disambiguationData":[TD([[makeQuery(id+"F4.imprint","IMPRINT",EDGE,{"derivedFrom":subQ0}),-1.0]])]});}
            var Q39;
            {var subQ0=sQuery(id+"F4.wireOp",EDGE,"E100");Q39=makeQuery(id+"F4.imprint","IMPRINT",FACE,{"disambiguationData":[TD([[makeQuery(id+"F4.imprint","IMPRINT",EDGE,{"derivedFrom":subQ0}),1.0]])]});}
            var Q40;
            {var subQ0=sQuery(id+"F4.wireOp",EDGE,"E95");Q40=makeQuery(id+"F4.imprint","IMPRINT",FACE,{"disambiguationData":[TD([[makeQuery(id+"F4.imprint","IMPRINT",EDGE,{"derivedFrom":subQ0}),1.0]])]});}
            var Q41;
            {var subQ0=sQuery(id+"F4.wireOp",EDGE,"E95");Q41=makeQuery(id+"F4.imprint","IMPRINT",FACE,{"disambiguationData":[TD([[makeQuery(id+"F4.imprint","IMPRINT",EDGE,{"derivedFrom":subQ0}),-1.0]])]});}
            var Q42;
            {var subQ5=sQuery(id+"F4.wireOp",EDGE,"E69");Q42=makeQuery(id+"F4.imprint","IMPRINT",FACE,{"disambiguationData":[TD([[makeQuery(id+"F4.imprint","IMPRINT",EDGE,{"derivedFrom":subQ5}),1.0]])]});}
            var Q43;
            {var subQ1=sQuery(id+"F4.wireOp",EDGE,"E74");Q43=makeQuery(id+"F4.imprint","IMPRINT",FACE,{"disambiguationData":[TD([[makeQuery(id+"F4.imprint","IMPRINT",EDGE,{"derivedFrom":subQ1}),-1.0]])]});}
            var Q44;
            {var subQ1=sQuery(id+"F4.wireOp",EDGE,"E74");Q44=makeQuery(id+"F4.imprint","IMPRINT",FACE,{"disambiguationData":[TD([[makeQuery(id+"F4.imprint","IMPRINT",EDGE,{"derivedFrom":subQ1}),1.0]])]});}
            var Q45;
            {var subQ0=sQuery(id+"F4.wireOp",EDGE,"E115");var subQ1=sQuery(id+"F4.wireOp",EDGE,"E90");var subQ2=makeQuery(id+"F4.imprint","INTERSECT",VERTEX,{"derivedFrom":[subQ1,subQ0]});Q45=makeQuery(id+"F4.imprint","IMPRINT",FACE,{"disambiguationData":[TD([[makeQuery(id+"F4.imprint","IMPRINT",EDGE,{"disambiguationData":[TD([[subQ2,-1.0]])],"derivedFrom":subQ1}),1.0]])]});}
            var Q46;
            {var subQ0=sQuery(id+"F4.wireOp",EDGE,"E96");var subQ5=sQuery(id+"F4.wireOp",EDGE,"E101");var subQ6=makeQuery(id+"F4.imprint","INTERSECT",VERTEX,{"derivedFrom":[subQ0,subQ5]});Q46=makeQuery(id+"F4.imprint","IMPRINT",FACE,{"disambiguationData":[TD([[makeQuery(id+"F4.imprint","IMPRINT",EDGE,{"disambiguationData":[TD([[subQ6,-1.0]])],"derivedFrom":subQ5}),-1.0]])]});}
            var Q47;
            {var subQ0=sQuery(id+"F4.wireOp",EDGE,"E96");var subQ1=sQuery(id+"F4.wireOp",EDGE,"E90");var subQ2=makeQuery(id+"F4.imprint","INTERSECT",VERTEX,{"derivedFrom":[subQ1,subQ0]});Q47=makeQuery(id+"F4.imprint","IMPRINT",FACE,{"disambiguationData":[TD([[makeQuery(id+"F4.imprint","IMPRINT",EDGE,{"disambiguationData":[TD([[subQ2,-1.0]])],"derivedFrom":subQ1}),-1.0]])]});}
            var Q48;
            {var subQ0=sQuery(id+"F4.wireOp",EDGE,"E96");var subQ1=sQuery(id+"F4.wireOp",EDGE,"E90");var subQ2=makeQuery(id+"F4.imprint","INTERSECT",VERTEX,{"derivedFrom":[subQ1,subQ0]});Q48=makeQuery(id+"F4.imprint","IMPRINT",FACE,{"disambiguationData":[TD([[makeQuery(id+"F4.imprint","IMPRINT",EDGE,{"disambiguationData":[TD([[subQ2,-1.0]])],"derivedFrom":subQ1}),1.0]])]});}
            var Q49;
            {var subQ0=sQuery(id+"F4.wireOp",EDGE,"E117");var subQ1=sQuery(id+"F4.wireOp",EDGE,"E92");var subQ2=makeQuery(id+"F4.imprint","INTERSECT",VERTEX,{"derivedFrom":[subQ1,subQ0]});Q49=makeQuery(id+"F4.imprint","IMPRINT",FACE,{"disambiguationData":[TD([[makeQuery(id+"F4.imprint","IMPRINT",EDGE,{"disambiguationData":[TD([[subQ2,-1.0]])],"derivedFrom":subQ1}),-1.0]])]});}
            var Q50;
            {var subQ1=sQuery(id+"F4.wireOp",EDGE,"E93");Q50=makeQuery(id+"F4.imprint","IMPRINT",FACE,{"disambiguationData":[TD([[makeQuery(id+"F4.imprint","IMPRINT",EDGE,{"derivedFrom":subQ1}),-1.0]])]});}
            var Q51;
            {var subQ5=sQuery(id+"F4.wireOp",EDGE,"E93");Q51=makeQuery(id+"F4.imprint","IMPRINT",FACE,{"disambiguationData":[TD([[makeQuery(id+"F4.imprint","IMPRINT",EDGE,{"derivedFrom":subQ5}),1.0]])]});}
            var Q52;
            {var subQ2=sQuery(id+"F4.wireOp",EDGE,"E71");Q52=makeQuery(id+"F4.imprint","IMPRINT",FACE,{"disambiguationData":[TD([[makeQuery(id+"F4.imprint","IMPRINT",EDGE,{"derivedFrom":subQ2}),-1.0]])]});}
            var Q53;
            {var subQ0=sQuery(id+"F4.wireOp",EDGE,"E97");var subQ5=sQuery(id+"F4.wireOp",EDGE,"E103");var subQ7=makeQuery(id+"F4.imprint","INTERSECT",VERTEX,{"derivedFrom":[subQ0,subQ5]});Q53=makeQuery(id+"F4.imprint","IMPRINT",FACE,{"disambiguationData":[TD([[makeQuery(id+"F4.imprint","IMPRINT",EDGE,{"disambiguationData":[TD([[subQ7,-1.0]])],"derivedFrom":subQ5}),1.0]])]});}
            var Q54;
            {var subQ0=sQuery(id+"F4.wireOp",EDGE,"E97");var subQ1=sQuery(id+"F4.wireOp",EDGE,"E92");var subQ2=makeQuery(id+"F4.imprint","INTERSECT",VERTEX,{"derivedFrom":[subQ1,subQ0]});Q54=makeQuery(id+"F4.imprint","IMPRINT",FACE,{"disambiguationData":[TD([[makeQuery(id+"F4.imprint","IMPRINT",EDGE,{"disambiguationData":[TD([[subQ2,-1.0]])],"derivedFrom":subQ1}),1.0]])]});}
            var Q55;
            {var subQ0=sQuery(id+"F4.wireOp",EDGE,"E97");var subQ5=sQuery(id+"F4.wireOp",EDGE,"E92");var subQ6=makeQuery(id+"F4.imprint","INTERSECT",VERTEX,{"derivedFrom":[subQ5,subQ0]});Q55=makeQuery(id+"F4.imprint","IMPRINT",FACE,{"disambiguationData":[TD([[makeQuery(id+"F4.imprint","IMPRINT",EDGE,{"disambiguationData":[TD([[subQ6,-1.0]])],"derivedFrom":subQ5}),-1.0]])]});}
            var Q56;
            Q56=makeQuery(id+"F4.imprint","IMPRINT",FACE,{"disambiguationData":[TD([[makeQuery(id+"F4.imprint","IMPRINT",EDGE,{"derivedFrom":sQuery(id+"F4.wireOp",EDGE,"E132")}),-1.0]])]});
            extrude(context, id + "F7", {"entities" : qUnion([Q0, Q1, Q2, Q3, Q4, Q5, Q6, Q7, Q8, Q9, Q10, Q11, Q12, Q13, Q14, Q15, Q16, Q17, Q18, Q19, Q20, Q21, Q22, Q23, Q24, Q25, Q26, Q27, Q28, Q29, Q30, Q31, Q32, Q33, Q34, Q35, Q36, Q37, Q38, Q39, Q40, Q41, Q42, Q43, Q44, Q45, Q46, Q47, Q48, Q49, Q50, Q51, Q52, Q53, Q54, Q55, Q56]), "operationType" : NewBodyOperationType.REMOVE, "oppositeDirection" : true, "depth" : 1.27 * mm});
        }
        {
            var Q0;
            Q0=makeQuery(id+"F7.boolean.opBoolean","COPY",FACE,{"derivedFrom":makeQuery(id+"F7.opExtrude","CAP_FACE",FACE,{"disambiguationData":[OSD([sQuery(id+"F4.wireOp",EDGE,"E139"),sQuery(id+"F4.wireOp",EDGE,"E140"),sQuery(id+"F4.wireOp",EDGE,"E141"),sQuery(id+"F4.wireOp",EDGE,"E142"),sQuery(id+"F4.wireOp",EDGE,"E143"),sQuery(id+"F4.wireOp",EDGE,"E144"),sQuery(id+"F4.wireOp",EDGE,"E147"),sQuery(id+"F4.wireOp",EDGE,"E149"),sQuery(id+"F4.wireOp",EDGE,"E177"),sQuery(id+"F4.wireOp",EDGE,"E193"),sQuery(id+"F4.wireOp",EDGE,"E201"),sQuery(id+"F4.wireOp",EDGE,"E202"),sQuery(id+"F4.wireOp",EDGE,"E203")])],"isStart":false})});
            var sketch = newSketch(context, id + "F8", { "sketchPlane" : qUnion([Q0])});
            skLineSegment(sketch, "E207", {"start": v(15.87, 20.02) * mm, "end": v(15.87, 35.76) * mm});
            skLineSegment(sketch, "E208", {"start": v(8.86, 29.41) * mm, "end": v(22.9, 29.41) * mm});
            skLineSegment(sketch, "E209", {"start": v(15.87, 29.41) * mm, "end": v(15.87, 20.02) * mm});
            skLineSegment(sketch, "E210", {"start": v(15.87, 24.71) * mm, "end": v(15.87, 29.41) * mm});
            skLineSegment(sketch, "E211", {"start": v(15.87, 27.06) * mm, "end": v(15.87, 24.71) * mm});
            skLineSegment(sketch, "E212", {"start": v(15.87, 25.89) * mm, "end": v(13.94, 25.89) * mm});
            skLineSegment(sketch, "E213", {"start": v(15.87, 25.89) * mm, "end": v(17.8, 25.89) * mm});
            skLineSegment(sketch, "E214", {"start": v(13.94, 25.89) * mm, "end": v(13.94, 25.5) * mm});
            skLineSegment(sketch, "E215", {"start": v(17.8, 25.89) * mm, "end": v(17.8, 25.5) * mm});
            skLineSegment(sketch, "E216", {"start": v(17.8, 25.5) * mm, "end": v(15.87, 25.89) * mm});
            skLineSegment(sketch, "E217", {"start": v(13.94, 25.5) * mm, "end": v(15.87, 25.89) * mm});
            skArc(sketch, "E218", {"start": v(15.87, 29.41) * mm, "mid": v(14.4, 27.7) * mm, "end": v(13.94, 25.5) * mm});
            skArc(sketch, "E219", {"start": v(17.8, 25.5) * mm, "mid": v(17.34, 27.7) * mm, "end": v(15.87, 29.41) * mm});
            skSolve(sketch);
        }
        {
            var Q0;
            Q0 = qSketchRegion(id + "F8", true);
            extrude(context, id + "F9", {"entities" : qUnion([Q0]), "operationType" : NewBodyOperationType.ADD, "depth" : 1.27 * mm});
        }
        {
            var Q0;
            Q0=makeQuery(id+"F7.boolean.opBoolean","COPY",FACE,{"derivedFrom":makeQuery(id+"F7.opExtrude","CAP_FACE",FACE,{"disambiguationData":[OSD([sQuery(id+"F4.wireOp",EDGE,"E139"),sQuery(id+"F4.wireOp",EDGE,"E140"),sQuery(id+"F4.wireOp",EDGE,"E141"),sQuery(id+"F4.wireOp",EDGE,"E142"),sQuery(id+"F4.wireOp",EDGE,"E143"),sQuery(id+"F4.wireOp",EDGE,"E144"),sQuery(id+"F4.wireOp",EDGE,"E147"),sQuery(id+"F4.wireOp",EDGE,"E149"),sQuery(id+"F4.wireOp",EDGE,"E177"),sQuery(id+"F4.wireOp",EDGE,"E193"),sQuery(id+"F4.wireOp",EDGE,"E201"),sQuery(id+"F4.wireOp",EDGE,"E202"),sQuery(id+"F4.wireOp",EDGE,"E203")])],"isStart":false})});
            var sketch = newSketch(context, id + "F10", { "sketchPlane" : qUnion([Q0])});
            skLineSegment(sketch, "E220", {"start": v(8.86, 29.41) * mm, "end": v(22.9, 29.41) * mm});
            skLineSegment(sketch, "E221", {"start": v(15.87, 35.76) * mm, "end": v(15.87, 29.41) * mm});
            skArc(sketch, "E222", {"start": v(15.87, 35.76) * mm, "mid": v(11.13, 33.96) * mm, "end": v(8.86, 29.41) * mm});
            skArc(sketch, "E223", {"start": v(22.9, 29.41) * mm, "mid": v(20.62, 33.96) * mm, "end": v(15.87, 35.76) * mm});
            skLineSegment(sketch, "E224", {"start": v(8.86, 29.41) * mm, "end": v(15.87, 29.41) * mm});
            skLineSegment(sketch, "E225", {"start": v(15.87, 29.41) * mm, "end": v(22.9, 29.41) * mm});
            skLineSegment(sketch, "E226", {"start": v(12.37, 29.41) * mm, "end": v(12.37, 34.83) * mm});
            skLineSegment(sketch, "E227", {"start": v(19.38, 29.41) * mm, "end": v(19.38, 34.83) * mm});
            skLineSegment(sketch, "E228", {"start": v(8.86, 29.41) * mm, "end": v(12.37, 29.41) * mm});
            skLineSegment(sketch, "E229", {"start": v(10.61, 29.41) * mm, "end": v(8.86, 29.41) * mm});
            skLineSegment(sketch, "E230", {"start": v(9.74, 29.41) * mm, "end": v(10.61, 29.41) * mm});
            skLineSegment(sketch, "E231", {"start": v(10.17, 29.41) * mm, "end": v(10.17, 32.86) * mm});
            skLineSegment(sketch, "E232", {"start": v(19.38, 29.41) * mm, "end": v(22.9, 29.41) * mm});
            skLineSegment(sketch, "E233", {"start": v(21.14, 29.41) * mm, "end": v(22.9, 29.41) * mm});
            skLineSegment(sketch, "E234", {"start": v(22.01, 29.41) * mm, "end": v(21.14, 29.41) * mm});
            skLineSegment(sketch, "E235", {"start": v(21.58, 29.41) * mm, "end": v(21.58, 32.9) * mm});
            skLineSegment(sketch, "E236", {"start": v(10.17, 29.41) * mm, "end": v(10.17, 28.4) * mm});
            skLineSegment(sketch, "E237", {"start": v(10.17, 28.4) * mm, "end": v(10.8, 28.4) * mm});
            skLineSegment(sketch, "E238", {"start": v(21.58, 28.4) * mm, "end": v(21.58, 29.41) * mm});
            skLineSegment(sketch, "E239", {"start": v(8.86, 29.41) * mm, "end": v(8.86, 28.4) * mm});
            skLineSegment(sketch, "E240", {"start": v(8.86, 28.4) * mm, "end": v(10.17, 28.4) * mm});
            skLineSegment(sketch, "E241", {"start": v(21.58, 28.4) * mm, "end": v(22.9, 28.4) * mm});
            skLineSegment(sketch, "E242", {"start": v(22.9, 28.4) * mm, "end": v(22.9, 29.41) * mm});
            skLineSegment(sketch, "E243", {"start": v(15.87, 29.41) * mm, "end": v(15.24, 29.41) * mm});
            skLineSegment(sketch, "E244", {"start": v(15.24, 29.41) * mm, "end": v(15.24, 35.73) * mm});
            skLineSegment(sketch, "E245", {"start": v(15.87, 29.41) * mm, "end": v(16.5, 29.41) * mm});
            skLineSegment(sketch, "E246", {"start": v(16.5, 29.41) * mm, "end": v(16.5, 35.73) * mm});
            skLineSegment(sketch, "E247", {"start": v(15.87, 35.76) * mm, "end": v(15.87, 32.57) * mm});
            skPoint(sketch, "E247.endSnap0", {"position": v(15.24, 32.57) * mm});
            skLineSegment(sketch, "E248", {"start": v(15.87, 35.76) * mm, "end": v(15.87, 34.17) * mm});
            skLineSegment(sketch, "E249", {"start": v(15.87, 34.17) * mm, "end": v(15.24, 34.17) * mm});
            skLineSegment(sketch, "E250", {"start": v(15.24, 34.17) * mm, "end": v(16.5, 34.17) * mm});
            skLineSegment(sketch, "E251", {"start": v(15.87, 34.17) * mm, "end": v(15.87, 32.57) * mm});
            skLineSegment(sketch, "E252", {"start": v(15.87, 33.37) * mm, "end": v(16.5, 33.37) * mm});
            skLineSegment(sketch, "E253", {"start": v(16.5, 33.37) * mm, "end": v(15.24, 33.37) * mm});
            skArc(sketch, "E254", {"start": v(9.52, 28.4) * mm, "mid": v(13.5, 29.6) * mm, "end": v(15.24, 33.37) * mm});
            skLineSegment(sketch, "E255", {"start": v(12.37, 33.72) * mm, "end": v(12.37, 32.7) * mm});
            skLineSegment(sketch, "E256", {"start": v(12.37, 32.7) * mm, "end": v(14.9, 32.7) * mm});
            skLineSegment(sketch, "E257", {"start": v(14.9, 32.7) * mm, "end": v(12.37, 33.72) * mm});
            skLineSegment(sketch, "E258", {"start": v(14.9, 32.7) * mm, "end": v(15.1, 33.18) * mm});
            skLineSegment(sketch, "E259", {"start": v(15.1, 33.18) * mm, "end": v(13.44, 33.84) * mm});
            skArc(sketch, "E260.trimOffspring", {"start": v(12.37, 33.72) * mm, "mid": v(9.75, 31.7) * mm, "end": v(9.52, 28.4) * mm});
            skLineSegment(sketch, "E261", {"start": v(13.44, 33.84) * mm, "end": v(12.37, 34.27) * mm});
            skArc(sketch, "E262", {"start": v(16.5, 33.37) * mm, "mid": v(18.26, 29.6) * mm, "end": v(22.23, 28.4) * mm});
            skArc(sketch, "E263", {"start": v(22.23, 28.4) * mm, "mid": v(22, 31.7) * mm, "end": v(19.38, 33.72) * mm});
            skLineSegment(sketch, "E264", {"start": v(19.38, 33.72) * mm, "end": v(19.38, 32.7) * mm});
            skLineSegment(sketch, "E265", {"start": v(19.38, 32.7) * mm, "end": v(16.84, 32.7) * mm});
            skLineSegment(sketch, "E266", {"start": v(16.84, 32.7) * mm, "end": v(19.38, 33.72) * mm});
            skLineSegment(sketch, "E267", {"start": v(16.84, 32.7) * mm, "end": v(16.65, 33.18) * mm});
            skLineSegment(sketch, "E268", {"start": v(16.65, 33.18) * mm, "end": v(18.3, 33.84) * mm});
            skLineSegment(sketch, "E269", {"start": v(18.3, 33.84) * mm, "end": v(19.38, 34.27) * mm});
            skLineSegment(sketch, "E270", {"start": v(15.24, 34.17) * mm, "end": v(15.24, 33.37) * mm});
            skLineSegment(sketch, "E271", {"start": v(15.24, 33.77) * mm, "end": v(15.24, 33.37) * mm});
            skLineSegment(sketch, "E272", {"start": v(15.24, 33.57) * mm, "end": v(12.37, 34.27) * mm});
            skLineSegment(sketch, "E273", {"start": v(16.5, 34.17) * mm, "end": v(16.5, 33.37) * mm});
            skLineSegment(sketch, "E274", {"start": v(16.5, 33.77) * mm, "end": v(16.5, 33.37) * mm});
            skLineSegment(sketch, "E275", {"start": v(16.5, 33.57) * mm, "end": v(19.38, 34.27) * mm});
            skLineSegment(sketch, "E276.trimOffspring", {"start": v(20.94, 28.4) * mm, "end": v(21.58, 28.4) * mm});
            skSolve(sketch);
        }
        {
            var Q0;
            {var subQ0=sQuery(id+"F10.wireOp",EDGE,"E237");Q0=makeQuery(id+"F10.imprint","IMPRINT",FACE,{"disambiguationData":[TD([[makeQuery(id+"F10.imprint","IMPRINT",EDGE,{"derivedFrom":subQ0}),-1.0]])]});}
            var Q1;
            {var subQ0=sQuery(id+"F10.wireOp",EDGE,"E276.trimOffspring");Q1=makeQuery(id+"F10.imprint","IMPRINT",FACE,{"disambiguationData":[TD([[makeQuery(id+"F10.imprint","IMPRINT",EDGE,{"derivedFrom":subQ0}),-1.0]])]});}
            var Q2;
            {var subQ1=sQuery(id+"F10.wireOp",EDGE,"E236");Q2=makeQuery(id+"F10.imprint","IMPRINT",FACE,{"disambiguationData":[TD([[makeQuery(id+"F10.imprint","IMPRINT",EDGE,{"derivedFrom":subQ1}),-1.0]])]});}
            var Q3;
            {var subQ1=sQuery(id+"F10.wireOp",EDGE,"E238");Q3=makeQuery(id+"F10.imprint","IMPRINT",FACE,{"disambiguationData":[TD([[makeQuery(id+"F10.imprint","IMPRINT",EDGE,{"derivedFrom":subQ1}),-1.0]])]});}
            var Q4;
            {var subQ2=sQuery(id+"F10.wireOp",EDGE,"E228");Q4=makeQuery(id+"F10.imprint","IMPRINT",FACE,{"disambiguationData":[TD([[makeQuery(id+"F10.imprint","IMPRINT",EDGE,{"derivedFrom":subQ2}),-1.0]])]});}
            var Q5;
            {var subQ1=sQuery(id+"F10.wireOp",EDGE,"E232");Q5=makeQuery(id+"F10.imprint","IMPRINT",FACE,{"disambiguationData":[TD([[makeQuery(id+"F10.imprint","IMPRINT",EDGE,{"derivedFrom":subQ1}),-1.0]])]});}
            var Q6;
            {var subQ0=sQuery(id+"F10.wireOp",EDGE,"E256");Q6=makeQuery(id+"F10.imprint","IMPRINT",FACE,{"disambiguationData":[TD([[makeQuery(id+"F10.imprint","IMPRINT",EDGE,{"derivedFrom":subQ0}),-1.0]])]});}
            var Q7;
            {var subQ0=sQuery(id+"F10.wireOp",EDGE,"E265");Q7=makeQuery(id+"F10.imprint","IMPRINT",FACE,{"disambiguationData":[TD([[makeQuery(id+"F10.imprint","IMPRINT",EDGE,{"derivedFrom":subQ0}),1.0]])]});}
            var Q8;
            {var subQ0=sQuery(id+"F10.wireOp",EDGE,"E223");var subQ3=sQuery(id+"F10.wireOp",EDGE,"E235");var subQ4=makeQuery(id+"F10.imprint","INTERSECT",VERTEX,{"derivedFrom":[subQ0,subQ3]});Q8=makeQuery(id+"F10.imprint","IMPRINT",FACE,{"disambiguationData":[TD([[makeQuery(id+"F10.imprint","IMPRINT",EDGE,{"disambiguationData":[TD([[subQ4,1.0]])],"derivedFrom":subQ3}),-1.0]])]});}
            var Q9;
            {var subQ3=sQuery(id+"F10.wireOp",EDGE,"E223");var subQ5=sQuery(id+"F10.wireOp",EDGE,"E235");var subQ6=makeQuery(id+"F10.imprint","INTERSECT",VERTEX,{"derivedFrom":[subQ3,subQ5]});Q9=makeQuery(id+"F10.imprint","IMPRINT",FACE,{"disambiguationData":[TD([[makeQuery(id+"F10.imprint","IMPRINT",EDGE,{"disambiguationData":[TD([[subQ6,1.0]])],"derivedFrom":subQ5}),1.0]])]});}
            var Q10;
            {var subQ0=sQuery(id+"F10.wireOp",EDGE,"E222");Q10=makeQuery(id+"F10.imprint","IMPRINT",FACE,{"disambiguationData":[TD([[makeQuery(id+"F10.imprint","IMPRINT",EDGE,{"derivedFrom":subQ0}),1.0]])]});}
            var Q11;
            {var subQ5=sQuery(id+"F10.wireOp",EDGE,"E228");Q11=makeQuery(id+"F10.imprint","IMPRINT",FACE,{"disambiguationData":[TD([[makeQuery(id+"F10.imprint","IMPRINT",EDGE,{"derivedFrom":subQ5}),1.0]])]});}
            var Q12;
            {var subQ0=sQuery(id+"F10.wireOp",EDGE,"E230");var subQ1=sQuery(id+"F10.wireOp",EDGE,"E229");var subQ2=makeQuery(id+"F10.imprint","INTERSECT",VERTEX,{"derivedFrom":[subQ1,subQ0]});Q12=makeQuery(id+"F10.imprint","IMPRINT",FACE,{"disambiguationData":[TD([[makeQuery(id+"F10.imprint","IMPRINT",EDGE,{"disambiguationData":[TD([[subQ2,-1.0]])],"derivedFrom":subQ1}),-1.0]])]});}
            var Q13;
            Q13=makeQuery(id+"F10.imprint","IMPRINT",FACE,{"disambiguationData":[TD([[makeQuery(id+"F10.imprint","IMPRINT",EDGE,{"derivedFrom":sQuery(id+"F10.wireOp",EDGE,"E255")}),1.0]])]});
            var Q14;
            Q14=makeQuery(id+"F10.imprint","IMPRINT",FACE,{"disambiguationData":[TD([[makeQuery(id+"F10.imprint","IMPRINT",EDGE,{"derivedFrom":sQuery(id+"F10.wireOp",EDGE,"E264")}),-1.0]])]});
            var Q15;
            {var subQ5=sQuery(id+"F10.wireOp",EDGE,"E232");Q15=makeQuery(id+"F10.imprint","IMPRINT",FACE,{"disambiguationData":[TD([[makeQuery(id+"F10.imprint","IMPRINT",EDGE,{"derivedFrom":subQ5}),1.0]])]});}
            var Q16;
            {var subQ0=sQuery(id+"F10.wireOp",EDGE,"E234");var subQ1=sQuery(id+"F10.wireOp",EDGE,"E233");var subQ2=makeQuery(id+"F10.imprint","INTERSECT",VERTEX,{"derivedFrom":[subQ1,subQ0]});Q16=makeQuery(id+"F10.imprint","IMPRINT",FACE,{"disambiguationData":[TD([[makeQuery(id+"F10.imprint","IMPRINT",EDGE,{"disambiguationData":[TD([[subQ2,-1.0]])],"derivedFrom":subQ1}),1.0]])]});}
            extrude(context, id + "F11", {"entities" : qUnion([Q0, Q1, Q2, Q3, Q4, Q5, Q6, Q7, Q8, Q9, Q10, Q11, Q12, Q13, Q14, Q15, Q16]), "operationType" : NewBodyOperationType.ADD, "depth" : 1.27 * mm});
        }
        {
            var Q0;
            {var subQ0=sQuery(id+"F2.wireOp",EDGE,"E11.top");var subQ1=sQuery(id+"F2.wireOp",EDGE,"E11.left");var subQ2=sQuery(id+"F2.wireOp",EDGE,"E9");var subQ6=sQuery(id+"F2.wireOp",EDGE,"E17.trimOffspring");var subQ8=sQuery(id+"F2.wireOp",EDGE,"E26");var subQ11=sQuery(id+"F5.wireOp",EDGE,"E206.top");var subQ13=sQuery(id+"F2.wireOp",EDGE,"E24");var subQ14=sQuery(id+"F2.wireOp",EDGE,"E11.bottom");var subQ15=sQuery(id+"F2.wireOp",EDGE,"E20");var subQ16=sQuery(id+"F2.wireOp",EDGE,"E11.right");var subQ17=sQuery(id+"F2.wireOp",EDGE,"E12.2");var subQ18=sQuery(id+"F2.wireOp",EDGE,"E19");var subQ19=sQuery(id+"F2.wireOp",EDGE,"E21");var subQ20=sQuery(id+"F2.wireOp",EDGE,"E25");var subQ21=sQuery(id+"F2.wireOp",EDGE,"E29");var subQ22=sQuery(id+"F2.wireOp",EDGE,"E12.3");var subQ23=sQuery(id+"F2.wireOp",EDGE,"E27");var subQ24=sQuery(id+"F2.wireOp",EDGE,"E28");var subQ25=sQuery(id+"F2.wireOp",EDGE,"E18");Q0=makeQuery(id+"F7.boolean.opBoolean","SPLIT",FACE,{"disambiguationData":[TD([makeQuery(id+"F1.opExtrude","SWEPT_FACE",FACE,{"disambiguationData":[OSD([sQuery(id+"F0.wireOp",EDGE,"E0")])]})])],"derivedFrom":makeQuery(id+"F6.boolean.opBoolean","MERGE",FACE,{"derivedFrom":[makeQuery(id+"F3.opExtrude","CAP_FACE",FACE,{"disambiguationData":[OSD([subQ2,subQ14,subQ0,subQ1,subQ16,subQ17,subQ22,subQ6,subQ25,subQ18,subQ15,subQ19,subQ13,subQ20,subQ8,subQ23,subQ24,subQ21])],"isStart":false}),makeQuery(id+"F6.opExtrude","SWEPT_FACE",FACE,{"disambiguationData":[OSD([subQ11])]})]})});}
            var sketch = newSketch(context, id + "F12", { "sketchPlane" : qUnion([Q0])});
            skLineSegment(sketch, "E277", {"start": v(6.35, 31.75) * mm, "end": v(9.51, 31.75) * mm});
            skLineSegment(sketch, "E278", {"start": v(25.4, 31.75) * mm, "end": v(22.24, 31.75) * mm});
            skArc(sketch, "E279", {"start": v(22.24, 31.75) * mm, "mid": v(15.87, 35.75) * mm, "end": v(9.51, 31.75) * mm});
            skArc(sketch, "E280.0", {"start": v(23.62, 31.75) * mm, "mid": v(15.87, 37.02) * mm, "end": v(8.13, 31.75) * mm});
            skLineSegment(sketch, "E281", {"start": v(6.35, 31.75) * mm, "end": v(6.35, 44.45) * mm});
            skLineSegment(sketch, "E282", {"start": v(6.35, 44.45) * mm, "end": v(25.4, 44.45) * mm});
            skLineSegment(sketch, "E283", {"start": v(25.4, 44.45) * mm, "end": v(25.4, 31.75) * mm});
            skSolve(sketch);
        }
        {
            var Q0;
            {var subQ1=sQuery(id+"F12.wireOp",EDGE,"E280.0");Q0=makeQuery(id+"F12.imprint","IMPRINT",FACE,{"disambiguationData":[TD([[makeQuery(id+"F12.imprint","IMPRINT",EDGE,{"derivedFrom":subQ1}),-1.0]])]});}
            extrude(context, id + "F13", {"entities" : qUnion([Q0]), "operationType" : NewBodyOperationType.REMOVE, "oppositeDirection" : true, "depth" : 25.4 * mm});
        }
        {
            var Q0;
            {var subQ0=sQuery(id+"F2.wireOp",EDGE,"E11.top");var subQ1=sQuery(id+"F2.wireOp",EDGE,"E11.left");var subQ2=sQuery(id+"F2.wireOp",EDGE,"E9");var subQ6=sQuery(id+"F2.wireOp",EDGE,"E17.trimOffspring");var subQ8=sQuery(id+"F2.wireOp",EDGE,"E26");var subQ11=sQuery(id+"F5.wireOp",EDGE,"E206.top");var subQ13=sQuery(id+"F2.wireOp",EDGE,"E24");var subQ14=sQuery(id+"F2.wireOp",EDGE,"E11.bottom");var subQ15=sQuery(id+"F2.wireOp",EDGE,"E20");var subQ16=sQuery(id+"F2.wireOp",EDGE,"E11.right");var subQ17=sQuery(id+"F2.wireOp",EDGE,"E12.2");var subQ18=sQuery(id+"F2.wireOp",EDGE,"E19");var subQ19=sQuery(id+"F2.wireOp",EDGE,"E21");var subQ20=sQuery(id+"F2.wireOp",EDGE,"E25");var subQ21=sQuery(id+"F2.wireOp",EDGE,"E29");var subQ22=sQuery(id+"F2.wireOp",EDGE,"E12.3");var subQ23=sQuery(id+"F2.wireOp",EDGE,"E27");var subQ24=sQuery(id+"F2.wireOp",EDGE,"E28");var subQ25=sQuery(id+"F2.wireOp",EDGE,"E18");Q0=makeQuery(id+"F7.boolean.opBoolean","SPLIT",FACE,{"disambiguationData":[TD([makeQuery(id+"F1.opExtrude","SWEPT_FACE",FACE,{"disambiguationData":[OSD([sQuery(id+"F0.wireOp",EDGE,"E0")])]})])],"derivedFrom":makeQuery(id+"F6.boolean.opBoolean","MERGE",FACE,{"derivedFrom":[makeQuery(id+"F3.opExtrude","CAP_FACE",FACE,{"disambiguationData":[OSD([subQ2,subQ14,subQ0,subQ1,subQ16,subQ17,subQ22,subQ6,subQ25,subQ18,subQ15,subQ19,subQ13,subQ20,subQ8,subQ23,subQ24,subQ21])],"isStart":false}),makeQuery(id+"F6.opExtrude","SWEPT_FACE",FACE,{"disambiguationData":[OSD([subQ11])]})]})});}
            var sketch = newSketch(context, id + "F14", { "sketchPlane" : qUnion([Q0])});
            skLineSegment(sketch, "E284", {"start": v(0, 31.75) * mm, "end": v(1.52, 30.23) * mm});
            skLineSegment(sketch, "E285", {"start": v(0, 0) * mm, "end": v(0.76, 0.76) * mm});
            skLineSegment(sketch, "E286", {"start": v(30.99, 0.76) * mm, "end": v(31.75, 0) * mm});
            skLineSegment(sketch, "E287", {"start": v(31.75, 31.75) * mm, "end": v(30.99, 30.99) * mm});
            skLineSegment(sketch, "E288", {"start": v(0.76, 30.99) * mm, "end": v(0.76, 0.76) * mm});
            skLineSegment(sketch, "E289", {"start": v(0.76, 0.76) * mm, "end": v(30.99, 0.76) * mm});
            skLineSegment(sketch, "E290", {"start": v(30.99, 0.76) * mm, "end": v(30.99, 30.99) * mm});
            skLineSegment(sketch, "E291", {"start": v(30.99, 30.99) * mm, "end": v(23.62, 30.99) * mm});
            skLineSegment(sketch, "E292", {"start": v(8.13, 30.23) * mm, "end": v(8.13, 31.75) * mm});
            skLineSegment(sketch, "E293", {"start": v(23.62, 31.75) * mm, "end": v(23.62, 30.23) * mm});
            skLineSegment(sketch, "E294.trimOffspring", {"start": v(8.13, 30.99) * mm, "end": v(0.76, 30.99) * mm});
            skPoint(sketch, "E295.orphan", {"position": v(30.23, 30.23) * mm});
            skPoint(sketch, "E296.orphan", {"position": v(1.52, 1.52) * mm});
            skPoint(sketch, "E297.orphan", {"position": v(30.23, 1.52) * mm});
            skLineSegment(sketch, "E298", {"start": v(8.13, 30.23) * mm, "end": v(1.52, 30.23) * mm});
            skLineSegment(sketch, "E299", {"start": v(1.52, 1.52) * mm, "end": v(30.23, 1.52) * mm});
            skLineSegment(sketch, "E300", {"start": v(30.23, 30.23) * mm, "end": v(30.23, 1.52) * mm});
            skLineSegment(sketch, "E301", {"start": v(30.23, 30.23) * mm, "end": v(23.62, 30.23) * mm});
            skSolve(sketch);
        }
        {
            var Q0;
            Q0 = qSketchRegion(id + "F14", true);
            var Q1;
            {var subQ8=sQuery(id+"F14.wireOp",EDGE,"E288");Q1=makeQuery(id+"F14.imprint","IMPRINT",FACE,{"disambiguationData":[TD([[makeQuery(id+"F14.imprint","IMPRINT",EDGE,{"derivedFrom":subQ8}),1.0]])]});}
            extrude(context, id + "F15", {"entities" : qUnion([Q0, Q1]), "operationType" : NewBodyOperationType.REMOVE, "oppositeDirection" : true, "depth" : 0.64 * mm});
        }
        {
            var Q0;
            {var subQ0=sQuery(id+"F2.wireOp",EDGE,"E11.top");var subQ1=sQuery(id+"F2.wireOp",EDGE,"E11.left");var subQ2=sQuery(id+"F2.wireOp",EDGE,"E9");var subQ6=sQuery(id+"F2.wireOp",EDGE,"E17.trimOffspring");var subQ8=sQuery(id+"F2.wireOp",EDGE,"E26");var subQ11=sQuery(id+"F5.wireOp",EDGE,"E206.top");var subQ13=sQuery(id+"F2.wireOp",EDGE,"E24");var subQ14=sQuery(id+"F2.wireOp",EDGE,"E11.bottom");var subQ15=sQuery(id+"F2.wireOp",EDGE,"E20");var subQ16=sQuery(id+"F2.wireOp",EDGE,"E11.right");var subQ17=sQuery(id+"F2.wireOp",EDGE,"E12.2");var subQ18=sQuery(id+"F2.wireOp",EDGE,"E19");var subQ19=sQuery(id+"F2.wireOp",EDGE,"E21");var subQ20=sQuery(id+"F2.wireOp",EDGE,"E25");var subQ21=sQuery(id+"F2.wireOp",EDGE,"E29");var subQ22=sQuery(id+"F2.wireOp",EDGE,"E12.3");var subQ23=sQuery(id+"F2.wireOp",EDGE,"E27");var subQ24=sQuery(id+"F2.wireOp",EDGE,"E28");var subQ25=sQuery(id+"F2.wireOp",EDGE,"E18");Q0=makeQuery(id+"F7.boolean.opBoolean","SPLIT",FACE,{"disambiguationData":[TD([makeQuery(id+"F1.opExtrude","SWEPT_FACE",FACE,{"disambiguationData":[OSD([sQuery(id+"F0.wireOp",EDGE,"E0")])]})])],"derivedFrom":makeQuery(id+"F6.boolean.opBoolean","MERGE",FACE,{"derivedFrom":[makeQuery(id+"F3.opExtrude","CAP_FACE",FACE,{"disambiguationData":[OSD([subQ2,subQ14,subQ0,subQ1,subQ16,subQ17,subQ22,subQ6,subQ25,subQ18,subQ15,subQ19,subQ13,subQ20,subQ8,subQ23,subQ24,subQ21])],"isStart":false}),makeQuery(id+"F6.opExtrude","SWEPT_FACE",FACE,{"disambiguationData":[OSD([subQ11])]})]})});}
            var sketch = newSketch(context, id + "F16", { "sketchPlane" : qUnion([Q0])});
            skLineSegment(sketch, "E302", {"start": v(8.13, 29.41) * mm, "end": v(3.97, 27.78) * mm});
            skLineSegment(sketch, "E303", {"start": v(3.97, 27.78) * mm, "end": v(3.97, 7.46) * mm});
            skLineSegment(sketch, "E304", {"start": v(3.97, 7.46) * mm, "end": v(14.86, 1.52) * mm});
            skLineSegment(sketch, "E305", {"start": v(14.86, 1.52) * mm, "end": v(16.9, 1.52) * mm});
            skLineSegment(sketch, "E306", {"start": v(16.9, 1.52) * mm, "end": v(27.78, 7.46) * mm});
            skLineSegment(sketch, "E307", {"start": v(27.78, 7.46) * mm, "end": v(27.78, 27.78) * mm});
            skLineSegment(sketch, "E308", {"start": v(27.78, 27.78) * mm, "end": v(23.62, 29.41) * mm});
            skLineSegment(sketch, "E309.0", {"start": v(27.02, 27.26) * mm, "end": v(23.62, 28.6) * mm});
            skLineSegment(sketch, "E309.1", {"start": v(27.02, 7.91) * mm, "end": v(27.02, 27.26) * mm});
            skLineSegment(sketch, "E309.2", {"start": v(8.13, 28.6) * mm, "end": v(4.73, 27.26) * mm});
            skLineSegment(sketch, "E309.3", {"start": v(4.73, 27.26) * mm, "end": v(4.73, 7.91) * mm});
            skLineSegment(sketch, "E309.4", {"start": v(4.73, 7.91) * mm, "end": v(12.6, 3.62) * mm});
            skLineSegment(sketch, "E310", {"start": v(8.13, 29.41) * mm, "end": v(8.13, 28.6) * mm});
            skLineSegment(sketch, "E311", {"start": v(23.62, 29.41) * mm, "end": v(23.62, 28.6) * mm});
            skLineSegment(sketch, "E312", {"start": v(14.43, 2.63) * mm, "end": v(14.36, 2.63) * mm});
            skLineSegment(sketch, "E313", {"start": v(17.4, 2.63) * mm, "end": v(17.32, 2.63) * mm});
            skArc(sketch, "E314", {"start": v(17.4, 2.63) * mm, "mid": v(18.3, 3.07) * mm, "end": v(19.15, 3.62) * mm});
            skArc(sketch, "E315", {"start": v(12.6, 3.62) * mm, "mid": v(13.45, 3.07) * mm, "end": v(14.36, 2.63) * mm});
            skLineSegment(sketch, "E316.trimOffspring", {"start": v(19.15, 3.62) * mm, "end": v(27.02, 7.91) * mm});
            skLineSegment(sketch, "E317", {"start": v(14.43, 2.63) * mm, "end": v(17.32, 2.63) * mm});
            skSolve(sketch);
        }
        {
            var Q0;
            Q0 = qSketchRegion(id + "F16", true);
            extrude(context, id + "F17", {"entities" : qUnion([Q0]), "operationType" : NewBodyOperationType.REMOVE, "oppositeDirection" : true, "depth" : 0.64 * mm});
        }
        {
            var Q0;
            {var subQ0=sQuery(id+"F2.wireOp",EDGE,"E11.top");var subQ1=sQuery(id+"F2.wireOp",EDGE,"E11.left");var subQ2=sQuery(id+"F2.wireOp",EDGE,"E9");var subQ6=sQuery(id+"F2.wireOp",EDGE,"E17.trimOffspring");var subQ8=sQuery(id+"F2.wireOp",EDGE,"E26");var subQ11=sQuery(id+"F5.wireOp",EDGE,"E206.top");var subQ13=sQuery(id+"F2.wireOp",EDGE,"E24");var subQ14=sQuery(id+"F2.wireOp",EDGE,"E11.bottom");var subQ15=sQuery(id+"F2.wireOp",EDGE,"E20");var subQ16=sQuery(id+"F2.wireOp",EDGE,"E11.right");var subQ17=sQuery(id+"F2.wireOp",EDGE,"E12.2");var subQ18=sQuery(id+"F2.wireOp",EDGE,"E19");var subQ19=sQuery(id+"F2.wireOp",EDGE,"E21");var subQ20=sQuery(id+"F2.wireOp",EDGE,"E25");var subQ21=sQuery(id+"F2.wireOp",EDGE,"E29");var subQ22=sQuery(id+"F2.wireOp",EDGE,"E12.3");var subQ23=sQuery(id+"F2.wireOp",EDGE,"E27");var subQ24=sQuery(id+"F2.wireOp",EDGE,"E28");var subQ25=sQuery(id+"F2.wireOp",EDGE,"E18");Q0=makeQuery(id+"F7.boolean.opBoolean","SPLIT",FACE,{"disambiguationData":[TD([makeQuery(id+"F1.opExtrude","SWEPT_FACE",FACE,{"disambiguationData":[OSD([sQuery(id+"F0.wireOp",EDGE,"E0")])]})])],"derivedFrom":makeQuery(id+"F6.boolean.opBoolean","MERGE",FACE,{"derivedFrom":[makeQuery(id+"F3.opExtrude","CAP_FACE",FACE,{"disambiguationData":[OSD([subQ2,subQ14,subQ0,subQ1,subQ16,subQ17,subQ22,subQ6,subQ25,subQ18,subQ15,subQ19,subQ13,subQ20,subQ8,subQ23,subQ24,subQ21])],"isStart":false}),makeQuery(id+"F6.opExtrude","SWEPT_FACE",FACE,{"disambiguationData":[OSD([subQ11])]})]})});}
            var sketch = newSketch(context, id + "F18", { "sketchPlane" : qUnion([Q0])});
            skCircle(sketch, "E318", {"center": v(0, 31.75) * mm, "radius": 3.18 * mm});
            skSolve(sketch);
        }
        {
            var Q0;
            Q0 = qSketchRegion(id + "F18", true);
            extrude(context, id + "F19", {"entities" : qUnion([Q0]), "operationType" : NewBodyOperationType.ADD, "oppositeDirection" : true, "depth" : 4.44 * mm});
        }
        {
            var Q0;
            {var subQ0=sQuery(id+"F2.wireOp",EDGE,"E11.top");var subQ1=sQuery(id+"F2.wireOp",EDGE,"E11.left");var subQ2=sQuery(id+"F2.wireOp",EDGE,"E9");var subQ6=sQuery(id+"F2.wireOp",EDGE,"E17.trimOffspring");var subQ8=sQuery(id+"F2.wireOp",EDGE,"E26");var subQ11=sQuery(id+"F5.wireOp",EDGE,"E206.top");var subQ13=sQuery(id+"F2.wireOp",EDGE,"E24");var subQ14=sQuery(id+"F2.wireOp",EDGE,"E11.bottom");var subQ15=sQuery(id+"F2.wireOp",EDGE,"E20");var subQ16=sQuery(id+"F2.wireOp",EDGE,"E11.right");var subQ17=sQuery(id+"F2.wireOp",EDGE,"E12.2");var subQ18=sQuery(id+"F2.wireOp",EDGE,"E19");var subQ19=sQuery(id+"F2.wireOp",EDGE,"E21");var subQ20=sQuery(id+"F2.wireOp",EDGE,"E25");var subQ21=sQuery(id+"F2.wireOp",EDGE,"E29");var subQ22=sQuery(id+"F2.wireOp",EDGE,"E12.3");var subQ23=sQuery(id+"F2.wireOp",EDGE,"E27");var subQ24=sQuery(id+"F2.wireOp",EDGE,"E28");var subQ25=sQuery(id+"F2.wireOp",EDGE,"E18");Q0=makeQuery(id+"F19.boolean.opBoolean","MERGE",FACE,{"derivedFrom":[makeQuery(id+"F7.boolean.opBoolean","SPLIT",FACE,{"disambiguationData":[TD([makeQuery(id+"F1.opExtrude","SWEPT_FACE",FACE,{"disambiguationData":[OSD([sQuery(id+"F0.wireOp",EDGE,"E0")])]})])],"derivedFrom":makeQuery(id+"F6.boolean.opBoolean","MERGE",FACE,{"derivedFrom":[makeQuery(id+"F3.opExtrude","CAP_FACE",FACE,{"disambiguationData":[OSD([subQ2,subQ14,subQ0,subQ1,subQ16,subQ17,subQ22,subQ6,subQ25,subQ18,subQ15,subQ19,subQ13,subQ20,subQ8,subQ23,subQ24,subQ21])],"isStart":false}),makeQuery(id+"F6.opExtrude","SWEPT_FACE",FACE,{"disambiguationData":[OSD([subQ11])]})]})}),makeQuery(id+"F19.opExtrude","CAP_FACE",FACE,{"disambiguationData":[OSD([sQuery(id+"F18.wireOp",EDGE,"E318")])],"isStart":true})]});}
            var sketch = newSketch(context, id + "F20", { "sketchPlane" : qUnion([Q0])});
            skCircle(sketch, "E319", {"center": v(0, 31.75) * mm, "radius": 2.29 * mm});
            skSolve(sketch);
        }
        {
            var Q0;
            Q0 = qSketchRegion(id + "F20", true);
            extrude(context, id + "F21", {"entities" : qUnion([Q0]), "operationType" : NewBodyOperationType.REMOVE, "oppositeDirection" : true, "depth" : 25.4 * mm});
        }
        {
            var Q0;
            Q0=makeQuery(id+"F7.boolean.opBoolean","COPY",FACE,{"derivedFrom":makeQuery(id+"F7.opExtrude","CAP_FACE",FACE,{"disambiguationData":[OSD([sQuery(id+"F4.wireOp",EDGE,"E139"),sQuery(id+"F4.wireOp",EDGE,"E140"),sQuery(id+"F4.wireOp",EDGE,"E141"),sQuery(id+"F4.wireOp",EDGE,"E142"),sQuery(id+"F4.wireOp",EDGE,"E143"),sQuery(id+"F4.wireOp",EDGE,"E144"),sQuery(id+"F4.wireOp",EDGE,"E147"),sQuery(id+"F4.wireOp",EDGE,"E149"),sQuery(id+"F4.wireOp",EDGE,"E177"),sQuery(id+"F4.wireOp",EDGE,"E193"),sQuery(id+"F4.wireOp",EDGE,"E201"),sQuery(id+"F4.wireOp",EDGE,"E202"),sQuery(id+"F4.wireOp",EDGE,"E203")])],"isStart":false})});
            var sketch = newSketch(context, id + "F22", { "sketchPlane" : qUnion([Q0])});
            skArc(sketch, "E320.0", {"start": v(15.87, 30.02) * mm, "mid": v(13.9, 27.82) * mm, "end": v(13.5, 24.9) * mm});
            skArc(sketch, "E320.1", {"start": v(18.26, 24.9) * mm, "mid": v(17.85, 27.82) * mm, "end": v(15.87, 30.02) * mm});
            skLineSegment(sketch, "E320.2", {"start": v(15.87, 25.37) * mm, "end": v(18.26, 24.9) * mm});
            skLineSegment(sketch, "E320.3", {"start": v(13.5, 24.9) * mm, "end": v(15.87, 25.37) * mm});
            skSolve(sketch);
        }
        {
            var Q0;
            Q0 = qSketchRegion(id + "F22", true);
            extrude(context, id + "F23", {"entities" : qUnion([Q0]), "operationType" : NewBodyOperationType.ADD, "depth" : 0.64 * mm});
        }
    });
